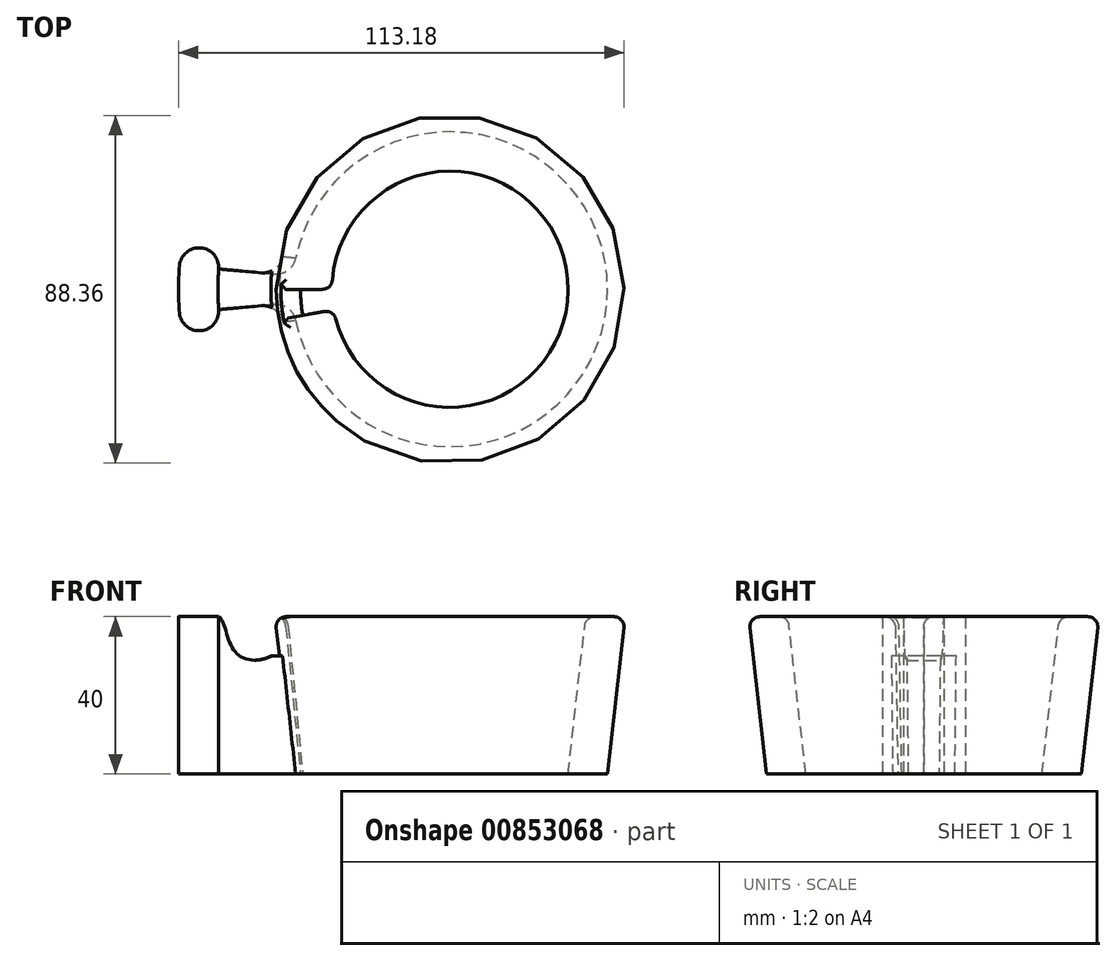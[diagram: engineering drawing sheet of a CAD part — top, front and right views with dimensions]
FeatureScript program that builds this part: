
annotation { "Feature Type Name" : "Feature", "Feature Type Description" : "" }
export const myFeature = defineFeature(function(context is Context, id is Id, definition is map)
    precondition{}
    {
        {
            var Q0;
            Q0=qCreatedBy(makeId("Front.planeOp"),FACE);
            var sketch = newSketch(context, id + "F0", { "sketchPlane" : qUnion([Q0])});
            skPoint(sketch, "E0", {"position": v(-30, 0) * mm});
            skPoint(sketch, "E1", {"position": v(-45, 134) * mm});
            skLineSegment(sketch, "E2", {"start": v(-34.48, 40) * mm, "end": v(-30, 0) * mm});
            skPoint(sketch, "E3", {"position": v(-34.48, 40) * mm});
            skLineSegment(sketch, "E4", {"start": v(-34.48, 40) * mm, "end": v(-44.48, 40) * mm});
            skLineSegment(sketch, "E5", {"start": v(-44.48, 40) * mm, "end": v(-40, 0) * mm});
            skLineSegment(sketch, "E6", {"start": v(-40, 0) * mm, "end": v(-30, 0) * mm});
            skLineSegment(sketch, "E7", {"start": v(0, 0) * mm, "end": v(0, 35.23) * mm});
            skSolve(sketch);
        }
        {
            var Q0;
            Q0=makeQuery(id+"F0.imprint","IMPRINT",FACE,{"disambiguationData":[TD([[makeQuery(id+"F0.imprint","IMPRINT",EDGE,{"derivedFrom":sQuery(id+"F0.wireOp",EDGE,"E2")}),-1.0]])]});
            var Q1;
            Q1=sQuery(id+"F0.wireOp",EDGE,"E7");
            revolve(context, id + "F1", {"surfaceOperationType" : NewSurfaceOperationType.NEW, "entities" : qUnion([Q0]), "axis" : qUnion([Q1]), "revolveType" : RevolveType.FULL});
        }
        {
            var Q0;
            Q0=qCreatedBy(makeId("Front.planeOp"),FACE);
            var sketch = newSketch(context, id + "F2", { "sketchPlane" : qUnion([Q0])});
            skPoint(sketch, "E8", {"position": v(-34, 40) * mm});
            skPoint(sketch, "E9", {"position": v(-30, 0) * mm});
            skLineSegment(sketch, "E10", {"start": v(-30, 0) * mm, "end": v(-34, 40) * mm});
            skLineSegment(sketch, "E11", {"start": v(-42, 40) * mm, "end": v(-38, 0) * mm});
            skLineSegment(sketch, "E12", {"start": v(-38, 0) * mm, "end": v(-30, 0) * mm});
            skLineSegment(sketch, "E13", {"start": v(-42, 40) * mm, "end": v(-34, 40) * mm});
            skSolve(sketch);
        }
        {
            var Q0;
            Q0 = qSketchRegion(id + "F2", true);
            var Q1;
            Q1=sQuery(id+"F0.wireOp",EDGE,"E7");
            revolve(context, id + "F3", {"operationType" : NewBodyOperationType.REMOVE, "surfaceOperationType" : NewSurfaceOperationType.NEW, "entities" : qUnion([Q0]), "axis" : qUnion([Q1]), "revolveType" : RevolveType.ONE_DIRECTION, "angle" : 10 * degree});
        }
        {
            var Q0;
            Q0=makeQuery(id+"F3.boolean.opBoolean","INTERSECT",EDGE,{"derivedFrom":[makeQuery(id+"F1.opRevolve","SWEPT_FACE",FACE,{"disambiguationData":[OSD([sQuery(id+"F0.wireOp",EDGE,"E2")])]}),makeQuery(id+"F3.opRevolve","CAP_FACE",FACE,{"disambiguationData":[OSD([sQuery(id+"F2.wireOp",EDGE,"E10"),sQuery(id+"F2.wireOp",EDGE,"E11"),sQuery(id+"F2.wireOp",EDGE,"E12"),sQuery(id+"F2.wireOp",EDGE,"E13")])],"isStart":true})]});
            var Q1;
            {var subQ0=sQuery(id+"F2.wireOp",EDGE,"E13");var subQ1=sQuery(id+"F2.wireOp",EDGE,"E12");var subQ2=sQuery(id+"F2.wireOp",EDGE,"E11");var subQ3=sQuery(id+"F2.wireOp",EDGE,"E10");var subQ6=makeQuery(id+"F3.boolean.opBoolean","COPY",FACE,{"derivedFrom":makeQuery(id+"F3.opRevolve","CAP_FACE",FACE,{"disambiguationData":[OSD([subQ3,subQ2,subQ1,subQ0])],"isStart":true})});Q1=makeQuery(id+"FKiHbmxaIrGreLf_1.19.F3.boolean.opBoolean","INTERSECT",EDGE,{"derivedFrom":[makeQuery(id+"FKiHbmxaIrGreLf_1.18.F3.boolean.opBoolean","SPLIT",FACE,{"disambiguationData":[TD([subQ6])],"derivedFrom":makeQuery(id+"FKiHbmxaIrGreLf_1.17.F3.boolean.opBoolean","SPLIT",FACE,{"disambiguationData":[TD([subQ6])],"derivedFrom":makeQuery(id+"FKiHbmxaIrGreLf_1.16.F3.boolean.opBoolean","SPLIT",FACE,{"disambiguationData":[TD([subQ6])],"derivedFrom":makeQuery(id+"FKiHbmxaIrGreLf_1.15.F3.boolean.opBoolean","SPLIT",FACE,{"disambiguationData":[TD([subQ6])],"derivedFrom":makeQuery(id+"FKiHbmxaIrGreLf_1.14.F3.boolean.opBoolean","SPLIT",FACE,{"disambiguationData":[TD([subQ6])],"derivedFrom":makeQuery(id+"FKiHbmxaIrGreLf_1.13.F3.boolean.opBoolean","SPLIT",FACE,{"disambiguationData":[TD([subQ6])],"derivedFrom":makeQuery(id+"FKiHbmxaIrGreLf_1.12.F3.boolean.opBoolean","SPLIT",FACE,{"disambiguationData":[TD([subQ6])],"derivedFrom":makeQuery(id+"FKiHbmxaIrGreLf_1.11.F3.boolean.opBoolean","SPLIT",FACE,{"disambiguationData":[TD([subQ6])],"derivedFrom":makeQuery(id+"FKiHbmxaIrGreLf_1.10.F3.boolean.opBoolean","SPLIT",FACE,{"disambiguationData":[TD([subQ6])],"derivedFrom":makeQuery(id+"FKiHbmxaIrGreLf_1.9.F3.boolean.opBoolean","SPLIT",FACE,{"disambiguationData":[TD([subQ6])],"derivedFrom":makeQuery(id+"FKiHbmxaIrGreLf_1.8.F3.boolean.opBoolean","SPLIT",FACE,{"disambiguationData":[TD([subQ6])],"derivedFrom":makeQuery(id+"FKiHbmxaIrGreLf_1.7.F3.boolean.opBoolean","SPLIT",FACE,{"disambiguationData":[TD([subQ6])],"derivedFrom":makeQuery(id+"FKiHbmxaIrGreLf_1.6.F3.boolean.opBoolean","SPLIT",FACE,{"disambiguationData":[TD([subQ6])],"derivedFrom":makeQuery(id+"FKiHbmxaIrGreLf_1.5.F3.boolean.opBoolean","SPLIT",FACE,{"disambiguationData":[TD([subQ6])],"derivedFrom":makeQuery(id+"FKiHbmxaIrGreLf_1.4.F3.boolean.opBoolean","SPLIT",FACE,{"disambiguationData":[TD([subQ6])],"derivedFrom":makeQuery(id+"FKiHbmxaIrGreLf_1.3.F3.boolean.opBoolean","SPLIT",FACE,{"disambiguationData":[TD([subQ6])],"derivedFrom":makeQuery(id+"FKiHbmxaIrGreLf_1.2.F3.boolean.opBoolean","SPLIT",FACE,{"disambiguationData":[TD([subQ6])],"derivedFrom":makeQuery(id+"FKiHbmxaIrGreLf_1.1.F3.boolean.opBoolean","SPLIT",FACE,{"disambiguationData":[TD([subQ6])],"derivedFrom":makeQuery(id+"F1.opRevolve","SWEPT_FACE",FACE,{"disambiguationData":[OSD([sQuery(id+"F0.wireOp",EDGE,"E2")])]})})})})})})})})})})})})})})})})})})}),makeQuery(id+"FKiHbmxaIrGreLf_1.19.F3.opRevolve","CAP_FACE",FACE,{"disambiguationData":[OSD([subQ3,subQ2,subQ1,subQ0])],"isStart":false})]});}
            var Q2;
            {var subQ0=sQuery(id+"F2.wireOp",EDGE,"E13");var subQ1=sQuery(id+"F2.wireOp",EDGE,"E12");var subQ2=sQuery(id+"F2.wireOp",EDGE,"E11");var subQ3=sQuery(id+"F2.wireOp",EDGE,"E10");var subQ6=makeQuery(id+"F3.boolean.opBoolean","COPY",FACE,{"derivedFrom":makeQuery(id+"F3.opRevolve","CAP_FACE",FACE,{"disambiguationData":[OSD([subQ3,subQ2,subQ1,subQ0])],"isStart":true})});Q2=makeQuery(id+"FKiHbmxaIrGreLf_1.19.F3.boolean.opBoolean","INTERSECT",EDGE,{"derivedFrom":[makeQuery(id+"FKiHbmxaIrGreLf_1.18.F3.boolean.opBoolean","SPLIT",FACE,{"disambiguationData":[TD([subQ6])],"derivedFrom":makeQuery(id+"FKiHbmxaIrGreLf_1.17.F3.boolean.opBoolean","SPLIT",FACE,{"disambiguationData":[TD([subQ6])],"derivedFrom":makeQuery(id+"FKiHbmxaIrGreLf_1.16.F3.boolean.opBoolean","SPLIT",FACE,{"disambiguationData":[TD([subQ6])],"derivedFrom":makeQuery(id+"FKiHbmxaIrGreLf_1.15.F3.boolean.opBoolean","SPLIT",FACE,{"disambiguationData":[TD([subQ6])],"derivedFrom":makeQuery(id+"FKiHbmxaIrGreLf_1.14.F3.boolean.opBoolean","SPLIT",FACE,{"disambiguationData":[TD([subQ6])],"derivedFrom":makeQuery(id+"FKiHbmxaIrGreLf_1.13.F3.boolean.opBoolean","SPLIT",FACE,{"disambiguationData":[TD([subQ6])],"derivedFrom":makeQuery(id+"FKiHbmxaIrGreLf_1.12.F3.boolean.opBoolean","SPLIT",FACE,{"disambiguationData":[TD([subQ6])],"derivedFrom":makeQuery(id+"FKiHbmxaIrGreLf_1.11.F3.boolean.opBoolean","SPLIT",FACE,{"disambiguationData":[TD([subQ6])],"derivedFrom":makeQuery(id+"FKiHbmxaIrGreLf_1.10.F3.boolean.opBoolean","SPLIT",FACE,{"disambiguationData":[TD([subQ6])],"derivedFrom":makeQuery(id+"FKiHbmxaIrGreLf_1.9.F3.boolean.opBoolean","SPLIT",FACE,{"disambiguationData":[TD([subQ6])],"derivedFrom":makeQuery(id+"FKiHbmxaIrGreLf_1.8.F3.boolean.opBoolean","SPLIT",FACE,{"disambiguationData":[TD([subQ6])],"derivedFrom":makeQuery(id+"FKiHbmxaIrGreLf_1.7.F3.boolean.opBoolean","SPLIT",FACE,{"disambiguationData":[TD([subQ6])],"derivedFrom":makeQuery(id+"FKiHbmxaIrGreLf_1.6.F3.boolean.opBoolean","SPLIT",FACE,{"disambiguationData":[TD([subQ6])],"derivedFrom":makeQuery(id+"FKiHbmxaIrGreLf_1.5.F3.boolean.opBoolean","SPLIT",FACE,{"disambiguationData":[TD([subQ6])],"derivedFrom":makeQuery(id+"FKiHbmxaIrGreLf_1.4.F3.boolean.opBoolean","SPLIT",FACE,{"disambiguationData":[TD([subQ6])],"derivedFrom":makeQuery(id+"FKiHbmxaIrGreLf_1.3.F3.boolean.opBoolean","SPLIT",FACE,{"disambiguationData":[TD([subQ6])],"derivedFrom":makeQuery(id+"FKiHbmxaIrGreLf_1.2.F3.boolean.opBoolean","SPLIT",FACE,{"disambiguationData":[TD([subQ6])],"derivedFrom":makeQuery(id+"FKiHbmxaIrGreLf_1.1.F3.boolean.opBoolean","SPLIT",FACE,{"disambiguationData":[TD([subQ6])],"derivedFrom":makeQuery(id+"F1.opRevolve","SWEPT_FACE",FACE,{"disambiguationData":[OSD([sQuery(id+"F0.wireOp",EDGE,"E2")])]})})})})})})})})})})})})})})})})})})}),makeQuery(id+"FKiHbmxaIrGreLf_1.19.F3.opRevolve","CAP_FACE",FACE,{"disambiguationData":[OSD([subQ3,subQ2,subQ1,subQ0])],"isStart":true})]});}
            var Q3;
            {var subQ0=sQuery(id+"F2.wireOp",EDGE,"E13");var subQ1=sQuery(id+"F2.wireOp",EDGE,"E12");var subQ2=sQuery(id+"F2.wireOp",EDGE,"E11");var subQ3=sQuery(id+"F2.wireOp",EDGE,"E10");var subQ6=makeQuery(id+"F3.boolean.opBoolean","COPY",FACE,{"derivedFrom":makeQuery(id+"F3.opRevolve","CAP_FACE",FACE,{"disambiguationData":[OSD([subQ3,subQ2,subQ1,subQ0])],"isStart":true})});Q3=makeQuery(id+"FKiHbmxaIrGreLf_1.18.F3.boolean.opBoolean","INTERSECT",EDGE,{"derivedFrom":[makeQuery(id+"FKiHbmxaIrGreLf_1.17.F3.boolean.opBoolean","SPLIT",FACE,{"disambiguationData":[TD([subQ6])],"derivedFrom":makeQuery(id+"FKiHbmxaIrGreLf_1.16.F3.boolean.opBoolean","SPLIT",FACE,{"disambiguationData":[TD([subQ6])],"derivedFrom":makeQuery(id+"FKiHbmxaIrGreLf_1.15.F3.boolean.opBoolean","SPLIT",FACE,{"disambiguationData":[TD([subQ6])],"derivedFrom":makeQuery(id+"FKiHbmxaIrGreLf_1.14.F3.boolean.opBoolean","SPLIT",FACE,{"disambiguationData":[TD([subQ6])],"derivedFrom":makeQuery(id+"FKiHbmxaIrGreLf_1.13.F3.boolean.opBoolean","SPLIT",FACE,{"disambiguationData":[TD([subQ6])],"derivedFrom":makeQuery(id+"FKiHbmxaIrGreLf_1.12.F3.boolean.opBoolean","SPLIT",FACE,{"disambiguationData":[TD([subQ6])],"derivedFrom":makeQuery(id+"FKiHbmxaIrGreLf_1.11.F3.boolean.opBoolean","SPLIT",FACE,{"disambiguationData":[TD([subQ6])],"derivedFrom":makeQuery(id+"FKiHbmxaIrGreLf_1.10.F3.boolean.opBoolean","SPLIT",FACE,{"disambiguationData":[TD([subQ6])],"derivedFrom":makeQuery(id+"FKiHbmxaIrGreLf_1.9.F3.boolean.opBoolean","SPLIT",FACE,{"disambiguationData":[TD([subQ6])],"derivedFrom":makeQuery(id+"FKiHbmxaIrGreLf_1.8.F3.boolean.opBoolean","SPLIT",FACE,{"disambiguationData":[TD([subQ6])],"derivedFrom":makeQuery(id+"FKiHbmxaIrGreLf_1.7.F3.boolean.opBoolean","SPLIT",FACE,{"disambiguationData":[TD([subQ6])],"derivedFrom":makeQuery(id+"FKiHbmxaIrGreLf_1.6.F3.boolean.opBoolean","SPLIT",FACE,{"disambiguationData":[TD([subQ6])],"derivedFrom":makeQuery(id+"FKiHbmxaIrGreLf_1.5.F3.boolean.opBoolean","SPLIT",FACE,{"disambiguationData":[TD([subQ6])],"derivedFrom":makeQuery(id+"FKiHbmxaIrGreLf_1.4.F3.boolean.opBoolean","SPLIT",FACE,{"disambiguationData":[TD([subQ6])],"derivedFrom":makeQuery(id+"FKiHbmxaIrGreLf_1.3.F3.boolean.opBoolean","SPLIT",FACE,{"disambiguationData":[TD([subQ6])],"derivedFrom":makeQuery(id+"FKiHbmxaIrGreLf_1.2.F3.boolean.opBoolean","SPLIT",FACE,{"disambiguationData":[TD([subQ6])],"derivedFrom":makeQuery(id+"FKiHbmxaIrGreLf_1.1.F3.boolean.opBoolean","SPLIT",FACE,{"disambiguationData":[TD([subQ6])],"derivedFrom":makeQuery(id+"F1.opRevolve","SWEPT_FACE",FACE,{"disambiguationData":[OSD([sQuery(id+"F0.wireOp",EDGE,"E2")])]})})})})})})})})})})})})})})})})})}),makeQuery(id+"FKiHbmxaIrGreLf_1.18.F3.opRevolve","CAP_FACE",FACE,{"disambiguationData":[OSD([subQ3,subQ2,subQ1,subQ0])],"isStart":false})]});}
            var Q4;
            {var subQ0=sQuery(id+"F2.wireOp",EDGE,"E13");var subQ1=sQuery(id+"F2.wireOp",EDGE,"E12");var subQ2=sQuery(id+"F2.wireOp",EDGE,"E11");var subQ3=sQuery(id+"F2.wireOp",EDGE,"E10");var subQ6=makeQuery(id+"F3.boolean.opBoolean","COPY",FACE,{"derivedFrom":makeQuery(id+"F3.opRevolve","CAP_FACE",FACE,{"disambiguationData":[OSD([subQ3,subQ2,subQ1,subQ0])],"isStart":true})});Q4=makeQuery(id+"FKiHbmxaIrGreLf_1.18.F3.boolean.opBoolean","INTERSECT",EDGE,{"derivedFrom":[makeQuery(id+"FKiHbmxaIrGreLf_1.17.F3.boolean.opBoolean","SPLIT",FACE,{"disambiguationData":[TD([subQ6])],"derivedFrom":makeQuery(id+"FKiHbmxaIrGreLf_1.16.F3.boolean.opBoolean","SPLIT",FACE,{"disambiguationData":[TD([subQ6])],"derivedFrom":makeQuery(id+"FKiHbmxaIrGreLf_1.15.F3.boolean.opBoolean","SPLIT",FACE,{"disambiguationData":[TD([subQ6])],"derivedFrom":makeQuery(id+"FKiHbmxaIrGreLf_1.14.F3.boolean.opBoolean","SPLIT",FACE,{"disambiguationData":[TD([subQ6])],"derivedFrom":makeQuery(id+"FKiHbmxaIrGreLf_1.13.F3.boolean.opBoolean","SPLIT",FACE,{"disambiguationData":[TD([subQ6])],"derivedFrom":makeQuery(id+"FKiHbmxaIrGreLf_1.12.F3.boolean.opBoolean","SPLIT",FACE,{"disambiguationData":[TD([subQ6])],"derivedFrom":makeQuery(id+"FKiHbmxaIrGreLf_1.11.F3.boolean.opBoolean","SPLIT",FACE,{"disambiguationData":[TD([subQ6])],"derivedFrom":makeQuery(id+"FKiHbmxaIrGreLf_1.10.F3.boolean.opBoolean","SPLIT",FACE,{"disambiguationData":[TD([subQ6])],"derivedFrom":makeQuery(id+"FKiHbmxaIrGreLf_1.9.F3.boolean.opBoolean","SPLIT",FACE,{"disambiguationData":[TD([subQ6])],"derivedFrom":makeQuery(id+"FKiHbmxaIrGreLf_1.8.F3.boolean.opBoolean","SPLIT",FACE,{"disambiguationData":[TD([subQ6])],"derivedFrom":makeQuery(id+"FKiHbmxaIrGreLf_1.7.F3.boolean.opBoolean","SPLIT",FACE,{"disambiguationData":[TD([subQ6])],"derivedFrom":makeQuery(id+"FKiHbmxaIrGreLf_1.6.F3.boolean.opBoolean","SPLIT",FACE,{"disambiguationData":[TD([subQ6])],"derivedFrom":makeQuery(id+"FKiHbmxaIrGreLf_1.5.F3.boolean.opBoolean","SPLIT",FACE,{"disambiguationData":[TD([subQ6])],"derivedFrom":makeQuery(id+"FKiHbmxaIrGreLf_1.4.F3.boolean.opBoolean","SPLIT",FACE,{"disambiguationData":[TD([subQ6])],"derivedFrom":makeQuery(id+"FKiHbmxaIrGreLf_1.3.F3.boolean.opBoolean","SPLIT",FACE,{"disambiguationData":[TD([subQ6])],"derivedFrom":makeQuery(id+"FKiHbmxaIrGreLf_1.2.F3.boolean.opBoolean","SPLIT",FACE,{"disambiguationData":[TD([subQ6])],"derivedFrom":makeQuery(id+"FKiHbmxaIrGreLf_1.1.F3.boolean.opBoolean","SPLIT",FACE,{"disambiguationData":[TD([subQ6])],"derivedFrom":makeQuery(id+"F1.opRevolve","SWEPT_FACE",FACE,{"disambiguationData":[OSD([sQuery(id+"F0.wireOp",EDGE,"E2")])]})})})})})})})})})})})})})})})})})}),makeQuery(id+"FKiHbmxaIrGreLf_1.18.F3.opRevolve","CAP_FACE",FACE,{"disambiguationData":[OSD([subQ3,subQ2,subQ1,subQ0])],"isStart":true})]});}
            var Q5;
            {var subQ0=sQuery(id+"F2.wireOp",EDGE,"E13");var subQ1=sQuery(id+"F2.wireOp",EDGE,"E12");var subQ2=sQuery(id+"F2.wireOp",EDGE,"E11");var subQ3=sQuery(id+"F2.wireOp",EDGE,"E10");var subQ6=makeQuery(id+"F3.boolean.opBoolean","COPY",FACE,{"derivedFrom":makeQuery(id+"F3.opRevolve","CAP_FACE",FACE,{"disambiguationData":[OSD([subQ3,subQ2,subQ1,subQ0])],"isStart":true})});Q5=makeQuery(id+"FKiHbmxaIrGreLf_1.17.F3.boolean.opBoolean","INTERSECT",EDGE,{"derivedFrom":[makeQuery(id+"FKiHbmxaIrGreLf_1.16.F3.boolean.opBoolean","SPLIT",FACE,{"disambiguationData":[TD([subQ6])],"derivedFrom":makeQuery(id+"FKiHbmxaIrGreLf_1.15.F3.boolean.opBoolean","SPLIT",FACE,{"disambiguationData":[TD([subQ6])],"derivedFrom":makeQuery(id+"FKiHbmxaIrGreLf_1.14.F3.boolean.opBoolean","SPLIT",FACE,{"disambiguationData":[TD([subQ6])],"derivedFrom":makeQuery(id+"FKiHbmxaIrGreLf_1.13.F3.boolean.opBoolean","SPLIT",FACE,{"disambiguationData":[TD([subQ6])],"derivedFrom":makeQuery(id+"FKiHbmxaIrGreLf_1.12.F3.boolean.opBoolean","SPLIT",FACE,{"disambiguationData":[TD([subQ6])],"derivedFrom":makeQuery(id+"FKiHbmxaIrGreLf_1.11.F3.boolean.opBoolean","SPLIT",FACE,{"disambiguationData":[TD([subQ6])],"derivedFrom":makeQuery(id+"FKiHbmxaIrGreLf_1.10.F3.boolean.opBoolean","SPLIT",FACE,{"disambiguationData":[TD([subQ6])],"derivedFrom":makeQuery(id+"FKiHbmxaIrGreLf_1.9.F3.boolean.opBoolean","SPLIT",FACE,{"disambiguationData":[TD([subQ6])],"derivedFrom":makeQuery(id+"FKiHbmxaIrGreLf_1.8.F3.boolean.opBoolean","SPLIT",FACE,{"disambiguationData":[TD([subQ6])],"derivedFrom":makeQuery(id+"FKiHbmxaIrGreLf_1.7.F3.boolean.opBoolean","SPLIT",FACE,{"disambiguationData":[TD([subQ6])],"derivedFrom":makeQuery(id+"FKiHbmxaIrGreLf_1.6.F3.boolean.opBoolean","SPLIT",FACE,{"disambiguationData":[TD([subQ6])],"derivedFrom":makeQuery(id+"FKiHbmxaIrGreLf_1.5.F3.boolean.opBoolean","SPLIT",FACE,{"disambiguationData":[TD([subQ6])],"derivedFrom":makeQuery(id+"FKiHbmxaIrGreLf_1.4.F3.boolean.opBoolean","SPLIT",FACE,{"disambiguationData":[TD([subQ6])],"derivedFrom":makeQuery(id+"FKiHbmxaIrGreLf_1.3.F3.boolean.opBoolean","SPLIT",FACE,{"disambiguationData":[TD([subQ6])],"derivedFrom":makeQuery(id+"FKiHbmxaIrGreLf_1.2.F3.boolean.opBoolean","SPLIT",FACE,{"disambiguationData":[TD([subQ6])],"derivedFrom":makeQuery(id+"FKiHbmxaIrGreLf_1.1.F3.boolean.opBoolean","SPLIT",FACE,{"disambiguationData":[TD([subQ6])],"derivedFrom":makeQuery(id+"F1.opRevolve","SWEPT_FACE",FACE,{"disambiguationData":[OSD([sQuery(id+"F0.wireOp",EDGE,"E2")])]})})})})})})})})})})})})})})})})}),makeQuery(id+"FKiHbmxaIrGreLf_1.17.F3.opRevolve","CAP_FACE",FACE,{"disambiguationData":[OSD([subQ3,subQ2,subQ1,subQ0])],"isStart":false})]});}
            var Q6;
            {var subQ0=sQuery(id+"F2.wireOp",EDGE,"E13");var subQ1=sQuery(id+"F2.wireOp",EDGE,"E12");var subQ2=sQuery(id+"F2.wireOp",EDGE,"E11");var subQ3=sQuery(id+"F2.wireOp",EDGE,"E10");var subQ6=makeQuery(id+"F3.boolean.opBoolean","COPY",FACE,{"derivedFrom":makeQuery(id+"F3.opRevolve","CAP_FACE",FACE,{"disambiguationData":[OSD([subQ3,subQ2,subQ1,subQ0])],"isStart":true})});Q6=makeQuery(id+"FKiHbmxaIrGreLf_1.17.F3.boolean.opBoolean","INTERSECT",EDGE,{"derivedFrom":[makeQuery(id+"FKiHbmxaIrGreLf_1.16.F3.boolean.opBoolean","SPLIT",FACE,{"disambiguationData":[TD([subQ6])],"derivedFrom":makeQuery(id+"FKiHbmxaIrGreLf_1.15.F3.boolean.opBoolean","SPLIT",FACE,{"disambiguationData":[TD([subQ6])],"derivedFrom":makeQuery(id+"FKiHbmxaIrGreLf_1.14.F3.boolean.opBoolean","SPLIT",FACE,{"disambiguationData":[TD([subQ6])],"derivedFrom":makeQuery(id+"FKiHbmxaIrGreLf_1.13.F3.boolean.opBoolean","SPLIT",FACE,{"disambiguationData":[TD([subQ6])],"derivedFrom":makeQuery(id+"FKiHbmxaIrGreLf_1.12.F3.boolean.opBoolean","SPLIT",FACE,{"disambiguationData":[TD([subQ6])],"derivedFrom":makeQuery(id+"FKiHbmxaIrGreLf_1.11.F3.boolean.opBoolean","SPLIT",FACE,{"disambiguationData":[TD([subQ6])],"derivedFrom":makeQuery(id+"FKiHbmxaIrGreLf_1.10.F3.boolean.opBoolean","SPLIT",FACE,{"disambiguationData":[TD([subQ6])],"derivedFrom":makeQuery(id+"FKiHbmxaIrGreLf_1.9.F3.boolean.opBoolean","SPLIT",FACE,{"disambiguationData":[TD([subQ6])],"derivedFrom":makeQuery(id+"FKiHbmxaIrGreLf_1.8.F3.boolean.opBoolean","SPLIT",FACE,{"disambiguationData":[TD([subQ6])],"derivedFrom":makeQuery(id+"FKiHbmxaIrGreLf_1.7.F3.boolean.opBoolean","SPLIT",FACE,{"disambiguationData":[TD([subQ6])],"derivedFrom":makeQuery(id+"FKiHbmxaIrGreLf_1.6.F3.boolean.opBoolean","SPLIT",FACE,{"disambiguationData":[TD([subQ6])],"derivedFrom":makeQuery(id+"FKiHbmxaIrGreLf_1.5.F3.boolean.opBoolean","SPLIT",FACE,{"disambiguationData":[TD([subQ6])],"derivedFrom":makeQuery(id+"FKiHbmxaIrGreLf_1.4.F3.boolean.opBoolean","SPLIT",FACE,{"disambiguationData":[TD([subQ6])],"derivedFrom":makeQuery(id+"FKiHbmxaIrGreLf_1.3.F3.boolean.opBoolean","SPLIT",FACE,{"disambiguationData":[TD([subQ6])],"derivedFrom":makeQuery(id+"FKiHbmxaIrGreLf_1.2.F3.boolean.opBoolean","SPLIT",FACE,{"disambiguationData":[TD([subQ6])],"derivedFrom":makeQuery(id+"FKiHbmxaIrGreLf_1.1.F3.boolean.opBoolean","SPLIT",FACE,{"disambiguationData":[TD([subQ6])],"derivedFrom":makeQuery(id+"F1.opRevolve","SWEPT_FACE",FACE,{"disambiguationData":[OSD([sQuery(id+"F0.wireOp",EDGE,"E2")])]})})})})})})})})})})})})})})})})}),makeQuery(id+"FKiHbmxaIrGreLf_1.17.F3.opRevolve","CAP_FACE",FACE,{"disambiguationData":[OSD([subQ3,subQ2,subQ1,subQ0])],"isStart":true})]});}
            var Q7;
            {var subQ0=sQuery(id+"F2.wireOp",EDGE,"E13");var subQ1=sQuery(id+"F2.wireOp",EDGE,"E12");var subQ2=sQuery(id+"F2.wireOp",EDGE,"E11");var subQ3=sQuery(id+"F2.wireOp",EDGE,"E10");var subQ6=makeQuery(id+"F3.boolean.opBoolean","COPY",FACE,{"derivedFrom":makeQuery(id+"F3.opRevolve","CAP_FACE",FACE,{"disambiguationData":[OSD([subQ3,subQ2,subQ1,subQ0])],"isStart":true})});Q7=makeQuery(id+"FKiHbmxaIrGreLf_1.16.F3.boolean.opBoolean","INTERSECT",EDGE,{"derivedFrom":[makeQuery(id+"FKiHbmxaIrGreLf_1.15.F3.boolean.opBoolean","SPLIT",FACE,{"disambiguationData":[TD([subQ6])],"derivedFrom":makeQuery(id+"FKiHbmxaIrGreLf_1.14.F3.boolean.opBoolean","SPLIT",FACE,{"disambiguationData":[TD([subQ6])],"derivedFrom":makeQuery(id+"FKiHbmxaIrGreLf_1.13.F3.boolean.opBoolean","SPLIT",FACE,{"disambiguationData":[TD([subQ6])],"derivedFrom":makeQuery(id+"FKiHbmxaIrGreLf_1.12.F3.boolean.opBoolean","SPLIT",FACE,{"disambiguationData":[TD([subQ6])],"derivedFrom":makeQuery(id+"FKiHbmxaIrGreLf_1.11.F3.boolean.opBoolean","SPLIT",FACE,{"disambiguationData":[TD([subQ6])],"derivedFrom":makeQuery(id+"FKiHbmxaIrGreLf_1.10.F3.boolean.opBoolean","SPLIT",FACE,{"disambiguationData":[TD([subQ6])],"derivedFrom":makeQuery(id+"FKiHbmxaIrGreLf_1.9.F3.boolean.opBoolean","SPLIT",FACE,{"disambiguationData":[TD([subQ6])],"derivedFrom":makeQuery(id+"FKiHbmxaIrGreLf_1.8.F3.boolean.opBoolean","SPLIT",FACE,{"disambiguationData":[TD([subQ6])],"derivedFrom":makeQuery(id+"FKiHbmxaIrGreLf_1.7.F3.boolean.opBoolean","SPLIT",FACE,{"disambiguationData":[TD([subQ6])],"derivedFrom":makeQuery(id+"FKiHbmxaIrGreLf_1.6.F3.boolean.opBoolean","SPLIT",FACE,{"disambiguationData":[TD([subQ6])],"derivedFrom":makeQuery(id+"FKiHbmxaIrGreLf_1.5.F3.boolean.opBoolean","SPLIT",FACE,{"disambiguationData":[TD([subQ6])],"derivedFrom":makeQuery(id+"FKiHbmxaIrGreLf_1.4.F3.boolean.opBoolean","SPLIT",FACE,{"disambiguationData":[TD([subQ6])],"derivedFrom":makeQuery(id+"FKiHbmxaIrGreLf_1.3.F3.boolean.opBoolean","SPLIT",FACE,{"disambiguationData":[TD([subQ6])],"derivedFrom":makeQuery(id+"FKiHbmxaIrGreLf_1.2.F3.boolean.opBoolean","SPLIT",FACE,{"disambiguationData":[TD([subQ6])],"derivedFrom":makeQuery(id+"FKiHbmxaIrGreLf_1.1.F3.boolean.opBoolean","SPLIT",FACE,{"disambiguationData":[TD([subQ6])],"derivedFrom":makeQuery(id+"F1.opRevolve","SWEPT_FACE",FACE,{"disambiguationData":[OSD([sQuery(id+"F0.wireOp",EDGE,"E2")])]})})})})})})})})})})})})})})})}),makeQuery(id+"FKiHbmxaIrGreLf_1.16.F3.opRevolve","CAP_FACE",FACE,{"disambiguationData":[OSD([subQ3,subQ2,subQ1,subQ0])],"isStart":false})]});}
            var Q8;
            {var subQ0=sQuery(id+"F2.wireOp",EDGE,"E13");var subQ1=sQuery(id+"F2.wireOp",EDGE,"E12");var subQ2=sQuery(id+"F2.wireOp",EDGE,"E11");var subQ3=sQuery(id+"F2.wireOp",EDGE,"E10");var subQ6=makeQuery(id+"F3.boolean.opBoolean","COPY",FACE,{"derivedFrom":makeQuery(id+"F3.opRevolve","CAP_FACE",FACE,{"disambiguationData":[OSD([subQ3,subQ2,subQ1,subQ0])],"isStart":true})});Q8=makeQuery(id+"FKiHbmxaIrGreLf_1.16.F3.boolean.opBoolean","INTERSECT",EDGE,{"derivedFrom":[makeQuery(id+"FKiHbmxaIrGreLf_1.15.F3.boolean.opBoolean","SPLIT",FACE,{"disambiguationData":[TD([subQ6])],"derivedFrom":makeQuery(id+"FKiHbmxaIrGreLf_1.14.F3.boolean.opBoolean","SPLIT",FACE,{"disambiguationData":[TD([subQ6])],"derivedFrom":makeQuery(id+"FKiHbmxaIrGreLf_1.13.F3.boolean.opBoolean","SPLIT",FACE,{"disambiguationData":[TD([subQ6])],"derivedFrom":makeQuery(id+"FKiHbmxaIrGreLf_1.12.F3.boolean.opBoolean","SPLIT",FACE,{"disambiguationData":[TD([subQ6])],"derivedFrom":makeQuery(id+"FKiHbmxaIrGreLf_1.11.F3.boolean.opBoolean","SPLIT",FACE,{"disambiguationData":[TD([subQ6])],"derivedFrom":makeQuery(id+"FKiHbmxaIrGreLf_1.10.F3.boolean.opBoolean","SPLIT",FACE,{"disambiguationData":[TD([subQ6])],"derivedFrom":makeQuery(id+"FKiHbmxaIrGreLf_1.9.F3.boolean.opBoolean","SPLIT",FACE,{"disambiguationData":[TD([subQ6])],"derivedFrom":makeQuery(id+"FKiHbmxaIrGreLf_1.8.F3.boolean.opBoolean","SPLIT",FACE,{"disambiguationData":[TD([subQ6])],"derivedFrom":makeQuery(id+"FKiHbmxaIrGreLf_1.7.F3.boolean.opBoolean","SPLIT",FACE,{"disambiguationData":[TD([subQ6])],"derivedFrom":makeQuery(id+"FKiHbmxaIrGreLf_1.6.F3.boolean.opBoolean","SPLIT",FACE,{"disambiguationData":[TD([subQ6])],"derivedFrom":makeQuery(id+"FKiHbmxaIrGreLf_1.5.F3.boolean.opBoolean","SPLIT",FACE,{"disambiguationData":[TD([subQ6])],"derivedFrom":makeQuery(id+"FKiHbmxaIrGreLf_1.4.F3.boolean.opBoolean","SPLIT",FACE,{"disambiguationData":[TD([subQ6])],"derivedFrom":makeQuery(id+"FKiHbmxaIrGreLf_1.3.F3.boolean.opBoolean","SPLIT",FACE,{"disambiguationData":[TD([subQ6])],"derivedFrom":makeQuery(id+"FKiHbmxaIrGreLf_1.2.F3.boolean.opBoolean","SPLIT",FACE,{"disambiguationData":[TD([subQ6])],"derivedFrom":makeQuery(id+"FKiHbmxaIrGreLf_1.1.F3.boolean.opBoolean","SPLIT",FACE,{"disambiguationData":[TD([subQ6])],"derivedFrom":makeQuery(id+"F1.opRevolve","SWEPT_FACE",FACE,{"disambiguationData":[OSD([sQuery(id+"F0.wireOp",EDGE,"E2")])]})})})})})})})})})})})})})})})}),makeQuery(id+"FKiHbmxaIrGreLf_1.16.F3.opRevolve","CAP_FACE",FACE,{"disambiguationData":[OSD([subQ3,subQ2,subQ1,subQ0])],"isStart":true})]});}
            var Q9;
            {var subQ0=sQuery(id+"F2.wireOp",EDGE,"E13");var subQ1=sQuery(id+"F2.wireOp",EDGE,"E12");var subQ2=sQuery(id+"F2.wireOp",EDGE,"E11");var subQ3=sQuery(id+"F2.wireOp",EDGE,"E10");var subQ6=makeQuery(id+"F3.boolean.opBoolean","COPY",FACE,{"derivedFrom":makeQuery(id+"F3.opRevolve","CAP_FACE",FACE,{"disambiguationData":[OSD([subQ3,subQ2,subQ1,subQ0])],"isStart":true})});Q9=makeQuery(id+"FKiHbmxaIrGreLf_1.15.F3.boolean.opBoolean","INTERSECT",EDGE,{"derivedFrom":[makeQuery(id+"FKiHbmxaIrGreLf_1.14.F3.boolean.opBoolean","SPLIT",FACE,{"disambiguationData":[TD([subQ6])],"derivedFrom":makeQuery(id+"FKiHbmxaIrGreLf_1.13.F3.boolean.opBoolean","SPLIT",FACE,{"disambiguationData":[TD([subQ6])],"derivedFrom":makeQuery(id+"FKiHbmxaIrGreLf_1.12.F3.boolean.opBoolean","SPLIT",FACE,{"disambiguationData":[TD([subQ6])],"derivedFrom":makeQuery(id+"FKiHbmxaIrGreLf_1.11.F3.boolean.opBoolean","SPLIT",FACE,{"disambiguationData":[TD([subQ6])],"derivedFrom":makeQuery(id+"FKiHbmxaIrGreLf_1.10.F3.boolean.opBoolean","SPLIT",FACE,{"disambiguationData":[TD([subQ6])],"derivedFrom":makeQuery(id+"FKiHbmxaIrGreLf_1.9.F3.boolean.opBoolean","SPLIT",FACE,{"disambiguationData":[TD([subQ6])],"derivedFrom":makeQuery(id+"FKiHbmxaIrGreLf_1.8.F3.boolean.opBoolean","SPLIT",FACE,{"disambiguationData":[TD([subQ6])],"derivedFrom":makeQuery(id+"FKiHbmxaIrGreLf_1.7.F3.boolean.opBoolean","SPLIT",FACE,{"disambiguationData":[TD([subQ6])],"derivedFrom":makeQuery(id+"FKiHbmxaIrGreLf_1.6.F3.boolean.opBoolean","SPLIT",FACE,{"disambiguationData":[TD([subQ6])],"derivedFrom":makeQuery(id+"FKiHbmxaIrGreLf_1.5.F3.boolean.opBoolean","SPLIT",FACE,{"disambiguationData":[TD([subQ6])],"derivedFrom":makeQuery(id+"FKiHbmxaIrGreLf_1.4.F3.boolean.opBoolean","SPLIT",FACE,{"disambiguationData":[TD([subQ6])],"derivedFrom":makeQuery(id+"FKiHbmxaIrGreLf_1.3.F3.boolean.opBoolean","SPLIT",FACE,{"disambiguationData":[TD([subQ6])],"derivedFrom":makeQuery(id+"FKiHbmxaIrGreLf_1.2.F3.boolean.opBoolean","SPLIT",FACE,{"disambiguationData":[TD([subQ6])],"derivedFrom":makeQuery(id+"FKiHbmxaIrGreLf_1.1.F3.boolean.opBoolean","SPLIT",FACE,{"disambiguationData":[TD([subQ6])],"derivedFrom":makeQuery(id+"F1.opRevolve","SWEPT_FACE",FACE,{"disambiguationData":[OSD([sQuery(id+"F0.wireOp",EDGE,"E2")])]})})})})})})})})})})})})})})}),makeQuery(id+"FKiHbmxaIrGreLf_1.15.F3.opRevolve","CAP_FACE",FACE,{"disambiguationData":[OSD([subQ3,subQ2,subQ1,subQ0])],"isStart":false})]});}
            var Q10;
            {var subQ0=sQuery(id+"F2.wireOp",EDGE,"E13");var subQ1=sQuery(id+"F2.wireOp",EDGE,"E12");var subQ2=sQuery(id+"F2.wireOp",EDGE,"E11");var subQ3=sQuery(id+"F2.wireOp",EDGE,"E10");var subQ6=makeQuery(id+"F3.boolean.opBoolean","COPY",FACE,{"derivedFrom":makeQuery(id+"F3.opRevolve","CAP_FACE",FACE,{"disambiguationData":[OSD([subQ3,subQ2,subQ1,subQ0])],"isStart":true})});Q10=makeQuery(id+"FKiHbmxaIrGreLf_1.15.F3.boolean.opBoolean","INTERSECT",EDGE,{"derivedFrom":[makeQuery(id+"FKiHbmxaIrGreLf_1.14.F3.boolean.opBoolean","SPLIT",FACE,{"disambiguationData":[TD([subQ6])],"derivedFrom":makeQuery(id+"FKiHbmxaIrGreLf_1.13.F3.boolean.opBoolean","SPLIT",FACE,{"disambiguationData":[TD([subQ6])],"derivedFrom":makeQuery(id+"FKiHbmxaIrGreLf_1.12.F3.boolean.opBoolean","SPLIT",FACE,{"disambiguationData":[TD([subQ6])],"derivedFrom":makeQuery(id+"FKiHbmxaIrGreLf_1.11.F3.boolean.opBoolean","SPLIT",FACE,{"disambiguationData":[TD([subQ6])],"derivedFrom":makeQuery(id+"FKiHbmxaIrGreLf_1.10.F3.boolean.opBoolean","SPLIT",FACE,{"disambiguationData":[TD([subQ6])],"derivedFrom":makeQuery(id+"FKiHbmxaIrGreLf_1.9.F3.boolean.opBoolean","SPLIT",FACE,{"disambiguationData":[TD([subQ6])],"derivedFrom":makeQuery(id+"FKiHbmxaIrGreLf_1.8.F3.boolean.opBoolean","SPLIT",FACE,{"disambiguationData":[TD([subQ6])],"derivedFrom":makeQuery(id+"FKiHbmxaIrGreLf_1.7.F3.boolean.opBoolean","SPLIT",FACE,{"disambiguationData":[TD([subQ6])],"derivedFrom":makeQuery(id+"FKiHbmxaIrGreLf_1.6.F3.boolean.opBoolean","SPLIT",FACE,{"disambiguationData":[TD([subQ6])],"derivedFrom":makeQuery(id+"FKiHbmxaIrGreLf_1.5.F3.boolean.opBoolean","SPLIT",FACE,{"disambiguationData":[TD([subQ6])],"derivedFrom":makeQuery(id+"FKiHbmxaIrGreLf_1.4.F3.boolean.opBoolean","SPLIT",FACE,{"disambiguationData":[TD([subQ6])],"derivedFrom":makeQuery(id+"FKiHbmxaIrGreLf_1.3.F3.boolean.opBoolean","SPLIT",FACE,{"disambiguationData":[TD([subQ6])],"derivedFrom":makeQuery(id+"FKiHbmxaIrGreLf_1.2.F3.boolean.opBoolean","SPLIT",FACE,{"disambiguationData":[TD([subQ6])],"derivedFrom":makeQuery(id+"FKiHbmxaIrGreLf_1.1.F3.boolean.opBoolean","SPLIT",FACE,{"disambiguationData":[TD([subQ6])],"derivedFrom":makeQuery(id+"F1.opRevolve","SWEPT_FACE",FACE,{"disambiguationData":[OSD([sQuery(id+"F0.wireOp",EDGE,"E2")])]})})})})})})})})})})})})})})}),makeQuery(id+"FKiHbmxaIrGreLf_1.15.F3.opRevolve","CAP_FACE",FACE,{"disambiguationData":[OSD([subQ3,subQ2,subQ1,subQ0])],"isStart":true})]});}
            var Q11;
            {var subQ0=sQuery(id+"F2.wireOp",EDGE,"E13");var subQ1=sQuery(id+"F2.wireOp",EDGE,"E12");var subQ2=sQuery(id+"F2.wireOp",EDGE,"E11");var subQ3=sQuery(id+"F2.wireOp",EDGE,"E10");var subQ6=makeQuery(id+"F3.boolean.opBoolean","COPY",FACE,{"derivedFrom":makeQuery(id+"F3.opRevolve","CAP_FACE",FACE,{"disambiguationData":[OSD([subQ3,subQ2,subQ1,subQ0])],"isStart":true})});Q11=makeQuery(id+"FKiHbmxaIrGreLf_1.14.F3.boolean.opBoolean","INTERSECT",EDGE,{"derivedFrom":[makeQuery(id+"FKiHbmxaIrGreLf_1.13.F3.boolean.opBoolean","SPLIT",FACE,{"disambiguationData":[TD([subQ6])],"derivedFrom":makeQuery(id+"FKiHbmxaIrGreLf_1.12.F3.boolean.opBoolean","SPLIT",FACE,{"disambiguationData":[TD([subQ6])],"derivedFrom":makeQuery(id+"FKiHbmxaIrGreLf_1.11.F3.boolean.opBoolean","SPLIT",FACE,{"disambiguationData":[TD([subQ6])],"derivedFrom":makeQuery(id+"FKiHbmxaIrGreLf_1.10.F3.boolean.opBoolean","SPLIT",FACE,{"disambiguationData":[TD([subQ6])],"derivedFrom":makeQuery(id+"FKiHbmxaIrGreLf_1.9.F3.boolean.opBoolean","SPLIT",FACE,{"disambiguationData":[TD([subQ6])],"derivedFrom":makeQuery(id+"FKiHbmxaIrGreLf_1.8.F3.boolean.opBoolean","SPLIT",FACE,{"disambiguationData":[TD([subQ6])],"derivedFrom":makeQuery(id+"FKiHbmxaIrGreLf_1.7.F3.boolean.opBoolean","SPLIT",FACE,{"disambiguationData":[TD([subQ6])],"derivedFrom":makeQuery(id+"FKiHbmxaIrGreLf_1.6.F3.boolean.opBoolean","SPLIT",FACE,{"disambiguationData":[TD([subQ6])],"derivedFrom":makeQuery(id+"FKiHbmxaIrGreLf_1.5.F3.boolean.opBoolean","SPLIT",FACE,{"disambiguationData":[TD([subQ6])],"derivedFrom":makeQuery(id+"FKiHbmxaIrGreLf_1.4.F3.boolean.opBoolean","SPLIT",FACE,{"disambiguationData":[TD([subQ6])],"derivedFrom":makeQuery(id+"FKiHbmxaIrGreLf_1.3.F3.boolean.opBoolean","SPLIT",FACE,{"disambiguationData":[TD([subQ6])],"derivedFrom":makeQuery(id+"FKiHbmxaIrGreLf_1.2.F3.boolean.opBoolean","SPLIT",FACE,{"disambiguationData":[TD([subQ6])],"derivedFrom":makeQuery(id+"FKiHbmxaIrGreLf_1.1.F3.boolean.opBoolean","SPLIT",FACE,{"disambiguationData":[TD([subQ6])],"derivedFrom":makeQuery(id+"F1.opRevolve","SWEPT_FACE",FACE,{"disambiguationData":[OSD([sQuery(id+"F0.wireOp",EDGE,"E2")])]})})})})})})})})})})})})})}),makeQuery(id+"FKiHbmxaIrGreLf_1.14.F3.opRevolve","CAP_FACE",FACE,{"disambiguationData":[OSD([subQ3,subQ2,subQ1,subQ0])],"isStart":false})]});}
            var Q12;
            {var subQ0=sQuery(id+"F2.wireOp",EDGE,"E13");var subQ1=sQuery(id+"F2.wireOp",EDGE,"E12");var subQ2=sQuery(id+"F2.wireOp",EDGE,"E11");var subQ3=sQuery(id+"F2.wireOp",EDGE,"E10");var subQ6=makeQuery(id+"F3.boolean.opBoolean","COPY",FACE,{"derivedFrom":makeQuery(id+"F3.opRevolve","CAP_FACE",FACE,{"disambiguationData":[OSD([subQ3,subQ2,subQ1,subQ0])],"isStart":true})});Q12=makeQuery(id+"FKiHbmxaIrGreLf_1.14.F3.boolean.opBoolean","INTERSECT",EDGE,{"derivedFrom":[makeQuery(id+"FKiHbmxaIrGreLf_1.13.F3.boolean.opBoolean","SPLIT",FACE,{"disambiguationData":[TD([subQ6])],"derivedFrom":makeQuery(id+"FKiHbmxaIrGreLf_1.12.F3.boolean.opBoolean","SPLIT",FACE,{"disambiguationData":[TD([subQ6])],"derivedFrom":makeQuery(id+"FKiHbmxaIrGreLf_1.11.F3.boolean.opBoolean","SPLIT",FACE,{"disambiguationData":[TD([subQ6])],"derivedFrom":makeQuery(id+"FKiHbmxaIrGreLf_1.10.F3.boolean.opBoolean","SPLIT",FACE,{"disambiguationData":[TD([subQ6])],"derivedFrom":makeQuery(id+"FKiHbmxaIrGreLf_1.9.F3.boolean.opBoolean","SPLIT",FACE,{"disambiguationData":[TD([subQ6])],"derivedFrom":makeQuery(id+"FKiHbmxaIrGreLf_1.8.F3.boolean.opBoolean","SPLIT",FACE,{"disambiguationData":[TD([subQ6])],"derivedFrom":makeQuery(id+"FKiHbmxaIrGreLf_1.7.F3.boolean.opBoolean","SPLIT",FACE,{"disambiguationData":[TD([subQ6])],"derivedFrom":makeQuery(id+"FKiHbmxaIrGreLf_1.6.F3.boolean.opBoolean","SPLIT",FACE,{"disambiguationData":[TD([subQ6])],"derivedFrom":makeQuery(id+"FKiHbmxaIrGreLf_1.5.F3.boolean.opBoolean","SPLIT",FACE,{"disambiguationData":[TD([subQ6])],"derivedFrom":makeQuery(id+"FKiHbmxaIrGreLf_1.4.F3.boolean.opBoolean","SPLIT",FACE,{"disambiguationData":[TD([subQ6])],"derivedFrom":makeQuery(id+"FKiHbmxaIrGreLf_1.3.F3.boolean.opBoolean","SPLIT",FACE,{"disambiguationData":[TD([subQ6])],"derivedFrom":makeQuery(id+"FKiHbmxaIrGreLf_1.2.F3.boolean.opBoolean","SPLIT",FACE,{"disambiguationData":[TD([subQ6])],"derivedFrom":makeQuery(id+"FKiHbmxaIrGreLf_1.1.F3.boolean.opBoolean","SPLIT",FACE,{"disambiguationData":[TD([subQ6])],"derivedFrom":makeQuery(id+"F1.opRevolve","SWEPT_FACE",FACE,{"disambiguationData":[OSD([sQuery(id+"F0.wireOp",EDGE,"E2")])]})})})})})})})})})})})})})}),makeQuery(id+"FKiHbmxaIrGreLf_1.14.F3.opRevolve","CAP_FACE",FACE,{"disambiguationData":[OSD([subQ3,subQ2,subQ1,subQ0])],"isStart":true})]});}
            var Q13;
            {var subQ0=sQuery(id+"F2.wireOp",EDGE,"E13");var subQ1=sQuery(id+"F2.wireOp",EDGE,"E12");var subQ2=sQuery(id+"F2.wireOp",EDGE,"E11");var subQ3=sQuery(id+"F2.wireOp",EDGE,"E10");var subQ6=makeQuery(id+"F3.boolean.opBoolean","COPY",FACE,{"derivedFrom":makeQuery(id+"F3.opRevolve","CAP_FACE",FACE,{"disambiguationData":[OSD([subQ3,subQ2,subQ1,subQ0])],"isStart":true})});Q13=makeQuery(id+"FKiHbmxaIrGreLf_1.13.F3.boolean.opBoolean","INTERSECT",EDGE,{"derivedFrom":[makeQuery(id+"FKiHbmxaIrGreLf_1.12.F3.boolean.opBoolean","SPLIT",FACE,{"disambiguationData":[TD([subQ6])],"derivedFrom":makeQuery(id+"FKiHbmxaIrGreLf_1.11.F3.boolean.opBoolean","SPLIT",FACE,{"disambiguationData":[TD([subQ6])],"derivedFrom":makeQuery(id+"FKiHbmxaIrGreLf_1.10.F3.boolean.opBoolean","SPLIT",FACE,{"disambiguationData":[TD([subQ6])],"derivedFrom":makeQuery(id+"FKiHbmxaIrGreLf_1.9.F3.boolean.opBoolean","SPLIT",FACE,{"disambiguationData":[TD([subQ6])],"derivedFrom":makeQuery(id+"FKiHbmxaIrGreLf_1.8.F3.boolean.opBoolean","SPLIT",FACE,{"disambiguationData":[TD([subQ6])],"derivedFrom":makeQuery(id+"FKiHbmxaIrGreLf_1.7.F3.boolean.opBoolean","SPLIT",FACE,{"disambiguationData":[TD([subQ6])],"derivedFrom":makeQuery(id+"FKiHbmxaIrGreLf_1.6.F3.boolean.opBoolean","SPLIT",FACE,{"disambiguationData":[TD([subQ6])],"derivedFrom":makeQuery(id+"FKiHbmxaIrGreLf_1.5.F3.boolean.opBoolean","SPLIT",FACE,{"disambiguationData":[TD([subQ6])],"derivedFrom":makeQuery(id+"FKiHbmxaIrGreLf_1.4.F3.boolean.opBoolean","SPLIT",FACE,{"disambiguationData":[TD([subQ6])],"derivedFrom":makeQuery(id+"FKiHbmxaIrGreLf_1.3.F3.boolean.opBoolean","SPLIT",FACE,{"disambiguationData":[TD([subQ6])],"derivedFrom":makeQuery(id+"FKiHbmxaIrGreLf_1.2.F3.boolean.opBoolean","SPLIT",FACE,{"disambiguationData":[TD([subQ6])],"derivedFrom":makeQuery(id+"FKiHbmxaIrGreLf_1.1.F3.boolean.opBoolean","SPLIT",FACE,{"disambiguationData":[TD([subQ6])],"derivedFrom":makeQuery(id+"F1.opRevolve","SWEPT_FACE",FACE,{"disambiguationData":[OSD([sQuery(id+"F0.wireOp",EDGE,"E2")])]})})})})})})})})})})})})}),makeQuery(id+"FKiHbmxaIrGreLf_1.13.F3.opRevolve","CAP_FACE",FACE,{"disambiguationData":[OSD([subQ3,subQ2,subQ1,subQ0])],"isStart":false})]});}
            var Q14;
            {var subQ0=sQuery(id+"F2.wireOp",EDGE,"E13");var subQ1=sQuery(id+"F2.wireOp",EDGE,"E12");var subQ2=sQuery(id+"F2.wireOp",EDGE,"E11");var subQ3=sQuery(id+"F2.wireOp",EDGE,"E10");var subQ6=makeQuery(id+"F3.boolean.opBoolean","COPY",FACE,{"derivedFrom":makeQuery(id+"F3.opRevolve","CAP_FACE",FACE,{"disambiguationData":[OSD([subQ3,subQ2,subQ1,subQ0])],"isStart":true})});Q14=makeQuery(id+"FKiHbmxaIrGreLf_1.13.F3.boolean.opBoolean","INTERSECT",EDGE,{"derivedFrom":[makeQuery(id+"FKiHbmxaIrGreLf_1.12.F3.boolean.opBoolean","SPLIT",FACE,{"disambiguationData":[TD([subQ6])],"derivedFrom":makeQuery(id+"FKiHbmxaIrGreLf_1.11.F3.boolean.opBoolean","SPLIT",FACE,{"disambiguationData":[TD([subQ6])],"derivedFrom":makeQuery(id+"FKiHbmxaIrGreLf_1.10.F3.boolean.opBoolean","SPLIT",FACE,{"disambiguationData":[TD([subQ6])],"derivedFrom":makeQuery(id+"FKiHbmxaIrGreLf_1.9.F3.boolean.opBoolean","SPLIT",FACE,{"disambiguationData":[TD([subQ6])],"derivedFrom":makeQuery(id+"FKiHbmxaIrGreLf_1.8.F3.boolean.opBoolean","SPLIT",FACE,{"disambiguationData":[TD([subQ6])],"derivedFrom":makeQuery(id+"FKiHbmxaIrGreLf_1.7.F3.boolean.opBoolean","SPLIT",FACE,{"disambiguationData":[TD([subQ6])],"derivedFrom":makeQuery(id+"FKiHbmxaIrGreLf_1.6.F3.boolean.opBoolean","SPLIT",FACE,{"disambiguationData":[TD([subQ6])],"derivedFrom":makeQuery(id+"FKiHbmxaIrGreLf_1.5.F3.boolean.opBoolean","SPLIT",FACE,{"disambiguationData":[TD([subQ6])],"derivedFrom":makeQuery(id+"FKiHbmxaIrGreLf_1.4.F3.boolean.opBoolean","SPLIT",FACE,{"disambiguationData":[TD([subQ6])],"derivedFrom":makeQuery(id+"FKiHbmxaIrGreLf_1.3.F3.boolean.opBoolean","SPLIT",FACE,{"disambiguationData":[TD([subQ6])],"derivedFrom":makeQuery(id+"FKiHbmxaIrGreLf_1.2.F3.boolean.opBoolean","SPLIT",FACE,{"disambiguationData":[TD([subQ6])],"derivedFrom":makeQuery(id+"FKiHbmxaIrGreLf_1.1.F3.boolean.opBoolean","SPLIT",FACE,{"disambiguationData":[TD([subQ6])],"derivedFrom":makeQuery(id+"F1.opRevolve","SWEPT_FACE",FACE,{"disambiguationData":[OSD([sQuery(id+"F0.wireOp",EDGE,"E2")])]})})})})})})})})})})})})}),makeQuery(id+"FKiHbmxaIrGreLf_1.13.F3.opRevolve","CAP_FACE",FACE,{"disambiguationData":[OSD([subQ3,subQ2,subQ1,subQ0])],"isStart":true})]});}
            var Q15;
            {var subQ0=sQuery(id+"F2.wireOp",EDGE,"E13");var subQ1=sQuery(id+"F2.wireOp",EDGE,"E12");var subQ2=sQuery(id+"F2.wireOp",EDGE,"E11");var subQ3=sQuery(id+"F2.wireOp",EDGE,"E10");var subQ6=makeQuery(id+"F3.boolean.opBoolean","COPY",FACE,{"derivedFrom":makeQuery(id+"F3.opRevolve","CAP_FACE",FACE,{"disambiguationData":[OSD([subQ3,subQ2,subQ1,subQ0])],"isStart":true})});Q15=makeQuery(id+"FKiHbmxaIrGreLf_1.12.F3.boolean.opBoolean","INTERSECT",EDGE,{"derivedFrom":[makeQuery(id+"FKiHbmxaIrGreLf_1.11.F3.boolean.opBoolean","SPLIT",FACE,{"disambiguationData":[TD([subQ6])],"derivedFrom":makeQuery(id+"FKiHbmxaIrGreLf_1.10.F3.boolean.opBoolean","SPLIT",FACE,{"disambiguationData":[TD([subQ6])],"derivedFrom":makeQuery(id+"FKiHbmxaIrGreLf_1.9.F3.boolean.opBoolean","SPLIT",FACE,{"disambiguationData":[TD([subQ6])],"derivedFrom":makeQuery(id+"FKiHbmxaIrGreLf_1.8.F3.boolean.opBoolean","SPLIT",FACE,{"disambiguationData":[TD([subQ6])],"derivedFrom":makeQuery(id+"FKiHbmxaIrGreLf_1.7.F3.boolean.opBoolean","SPLIT",FACE,{"disambiguationData":[TD([subQ6])],"derivedFrom":makeQuery(id+"FKiHbmxaIrGreLf_1.6.F3.boolean.opBoolean","SPLIT",FACE,{"disambiguationData":[TD([subQ6])],"derivedFrom":makeQuery(id+"FKiHbmxaIrGreLf_1.5.F3.boolean.opBoolean","SPLIT",FACE,{"disambiguationData":[TD([subQ6])],"derivedFrom":makeQuery(id+"FKiHbmxaIrGreLf_1.4.F3.boolean.opBoolean","SPLIT",FACE,{"disambiguationData":[TD([subQ6])],"derivedFrom":makeQuery(id+"FKiHbmxaIrGreLf_1.3.F3.boolean.opBoolean","SPLIT",FACE,{"disambiguationData":[TD([subQ6])],"derivedFrom":makeQuery(id+"FKiHbmxaIrGreLf_1.2.F3.boolean.opBoolean","SPLIT",FACE,{"disambiguationData":[TD([subQ6])],"derivedFrom":makeQuery(id+"FKiHbmxaIrGreLf_1.1.F3.boolean.opBoolean","SPLIT",FACE,{"disambiguationData":[TD([subQ6])],"derivedFrom":makeQuery(id+"F1.opRevolve","SWEPT_FACE",FACE,{"disambiguationData":[OSD([sQuery(id+"F0.wireOp",EDGE,"E2")])]})})})})})})})})})})})}),makeQuery(id+"FKiHbmxaIrGreLf_1.12.F3.opRevolve","CAP_FACE",FACE,{"disambiguationData":[OSD([subQ3,subQ2,subQ1,subQ0])],"isStart":false})]});}
            var Q16;
            {var subQ0=sQuery(id+"F2.wireOp",EDGE,"E13");var subQ1=sQuery(id+"F2.wireOp",EDGE,"E12");var subQ2=sQuery(id+"F2.wireOp",EDGE,"E11");var subQ3=sQuery(id+"F2.wireOp",EDGE,"E10");var subQ6=makeQuery(id+"F3.boolean.opBoolean","COPY",FACE,{"derivedFrom":makeQuery(id+"F3.opRevolve","CAP_FACE",FACE,{"disambiguationData":[OSD([subQ3,subQ2,subQ1,subQ0])],"isStart":true})});Q16=makeQuery(id+"FKiHbmxaIrGreLf_1.12.F3.boolean.opBoolean","INTERSECT",EDGE,{"derivedFrom":[makeQuery(id+"FKiHbmxaIrGreLf_1.11.F3.boolean.opBoolean","SPLIT",FACE,{"disambiguationData":[TD([subQ6])],"derivedFrom":makeQuery(id+"FKiHbmxaIrGreLf_1.10.F3.boolean.opBoolean","SPLIT",FACE,{"disambiguationData":[TD([subQ6])],"derivedFrom":makeQuery(id+"FKiHbmxaIrGreLf_1.9.F3.boolean.opBoolean","SPLIT",FACE,{"disambiguationData":[TD([subQ6])],"derivedFrom":makeQuery(id+"FKiHbmxaIrGreLf_1.8.F3.boolean.opBoolean","SPLIT",FACE,{"disambiguationData":[TD([subQ6])],"derivedFrom":makeQuery(id+"FKiHbmxaIrGreLf_1.7.F3.boolean.opBoolean","SPLIT",FACE,{"disambiguationData":[TD([subQ6])],"derivedFrom":makeQuery(id+"FKiHbmxaIrGreLf_1.6.F3.boolean.opBoolean","SPLIT",FACE,{"disambiguationData":[TD([subQ6])],"derivedFrom":makeQuery(id+"FKiHbmxaIrGreLf_1.5.F3.boolean.opBoolean","SPLIT",FACE,{"disambiguationData":[TD([subQ6])],"derivedFrom":makeQuery(id+"FKiHbmxaIrGreLf_1.4.F3.boolean.opBoolean","SPLIT",FACE,{"disambiguationData":[TD([subQ6])],"derivedFrom":makeQuery(id+"FKiHbmxaIrGreLf_1.3.F3.boolean.opBoolean","SPLIT",FACE,{"disambiguationData":[TD([subQ6])],"derivedFrom":makeQuery(id+"FKiHbmxaIrGreLf_1.2.F3.boolean.opBoolean","SPLIT",FACE,{"disambiguationData":[TD([subQ6])],"derivedFrom":makeQuery(id+"FKiHbmxaIrGreLf_1.1.F3.boolean.opBoolean","SPLIT",FACE,{"disambiguationData":[TD([subQ6])],"derivedFrom":makeQuery(id+"F1.opRevolve","SWEPT_FACE",FACE,{"disambiguationData":[OSD([sQuery(id+"F0.wireOp",EDGE,"E2")])]})})})})})})})})})})})}),makeQuery(id+"FKiHbmxaIrGreLf_1.12.F3.opRevolve","CAP_FACE",FACE,{"disambiguationData":[OSD([subQ3,subQ2,subQ1,subQ0])],"isStart":true})]});}
            var Q17;
            {var subQ0=sQuery(id+"F2.wireOp",EDGE,"E13");var subQ1=sQuery(id+"F2.wireOp",EDGE,"E12");var subQ2=sQuery(id+"F2.wireOp",EDGE,"E11");var subQ3=sQuery(id+"F2.wireOp",EDGE,"E10");var subQ6=makeQuery(id+"F3.boolean.opBoolean","COPY",FACE,{"derivedFrom":makeQuery(id+"F3.opRevolve","CAP_FACE",FACE,{"disambiguationData":[OSD([subQ3,subQ2,subQ1,subQ0])],"isStart":true})});Q17=makeQuery(id+"FKiHbmxaIrGreLf_1.11.F3.boolean.opBoolean","INTERSECT",EDGE,{"derivedFrom":[makeQuery(id+"FKiHbmxaIrGreLf_1.10.F3.boolean.opBoolean","SPLIT",FACE,{"disambiguationData":[TD([subQ6])],"derivedFrom":makeQuery(id+"FKiHbmxaIrGreLf_1.9.F3.boolean.opBoolean","SPLIT",FACE,{"disambiguationData":[TD([subQ6])],"derivedFrom":makeQuery(id+"FKiHbmxaIrGreLf_1.8.F3.boolean.opBoolean","SPLIT",FACE,{"disambiguationData":[TD([subQ6])],"derivedFrom":makeQuery(id+"FKiHbmxaIrGreLf_1.7.F3.boolean.opBoolean","SPLIT",FACE,{"disambiguationData":[TD([subQ6])],"derivedFrom":makeQuery(id+"FKiHbmxaIrGreLf_1.6.F3.boolean.opBoolean","SPLIT",FACE,{"disambiguationData":[TD([subQ6])],"derivedFrom":makeQuery(id+"FKiHbmxaIrGreLf_1.5.F3.boolean.opBoolean","SPLIT",FACE,{"disambiguationData":[TD([subQ6])],"derivedFrom":makeQuery(id+"FKiHbmxaIrGreLf_1.4.F3.boolean.opBoolean","SPLIT",FACE,{"disambiguationData":[TD([subQ6])],"derivedFrom":makeQuery(id+"FKiHbmxaIrGreLf_1.3.F3.boolean.opBoolean","SPLIT",FACE,{"disambiguationData":[TD([subQ6])],"derivedFrom":makeQuery(id+"FKiHbmxaIrGreLf_1.2.F3.boolean.opBoolean","SPLIT",FACE,{"disambiguationData":[TD([subQ6])],"derivedFrom":makeQuery(id+"FKiHbmxaIrGreLf_1.1.F3.boolean.opBoolean","SPLIT",FACE,{"disambiguationData":[TD([subQ6])],"derivedFrom":makeQuery(id+"F1.opRevolve","SWEPT_FACE",FACE,{"disambiguationData":[OSD([sQuery(id+"F0.wireOp",EDGE,"E2")])]})})})})})})})})})})}),makeQuery(id+"FKiHbmxaIrGreLf_1.11.F3.opRevolve","CAP_FACE",FACE,{"disambiguationData":[OSD([subQ3,subQ2,subQ1,subQ0])],"isStart":false})]});}
            var Q18;
            {var subQ0=sQuery(id+"F2.wireOp",EDGE,"E13");var subQ1=sQuery(id+"F2.wireOp",EDGE,"E12");var subQ2=sQuery(id+"F2.wireOp",EDGE,"E11");var subQ3=sQuery(id+"F2.wireOp",EDGE,"E10");var subQ6=makeQuery(id+"F3.boolean.opBoolean","COPY",FACE,{"derivedFrom":makeQuery(id+"F3.opRevolve","CAP_FACE",FACE,{"disambiguationData":[OSD([subQ3,subQ2,subQ1,subQ0])],"isStart":true})});Q18=makeQuery(id+"FKiHbmxaIrGreLf_1.11.F3.boolean.opBoolean","INTERSECT",EDGE,{"derivedFrom":[makeQuery(id+"FKiHbmxaIrGreLf_1.10.F3.boolean.opBoolean","SPLIT",FACE,{"disambiguationData":[TD([subQ6])],"derivedFrom":makeQuery(id+"FKiHbmxaIrGreLf_1.9.F3.boolean.opBoolean","SPLIT",FACE,{"disambiguationData":[TD([subQ6])],"derivedFrom":makeQuery(id+"FKiHbmxaIrGreLf_1.8.F3.boolean.opBoolean","SPLIT",FACE,{"disambiguationData":[TD([subQ6])],"derivedFrom":makeQuery(id+"FKiHbmxaIrGreLf_1.7.F3.boolean.opBoolean","SPLIT",FACE,{"disambiguationData":[TD([subQ6])],"derivedFrom":makeQuery(id+"FKiHbmxaIrGreLf_1.6.F3.boolean.opBoolean","SPLIT",FACE,{"disambiguationData":[TD([subQ6])],"derivedFrom":makeQuery(id+"FKiHbmxaIrGreLf_1.5.F3.boolean.opBoolean","SPLIT",FACE,{"disambiguationData":[TD([subQ6])],"derivedFrom":makeQuery(id+"FKiHbmxaIrGreLf_1.4.F3.boolean.opBoolean","SPLIT",FACE,{"disambiguationData":[TD([subQ6])],"derivedFrom":makeQuery(id+"FKiHbmxaIrGreLf_1.3.F3.boolean.opBoolean","SPLIT",FACE,{"disambiguationData":[TD([subQ6])],"derivedFrom":makeQuery(id+"FKiHbmxaIrGreLf_1.2.F3.boolean.opBoolean","SPLIT",FACE,{"disambiguationData":[TD([subQ6])],"derivedFrom":makeQuery(id+"FKiHbmxaIrGreLf_1.1.F3.boolean.opBoolean","SPLIT",FACE,{"disambiguationData":[TD([subQ6])],"derivedFrom":makeQuery(id+"F1.opRevolve","SWEPT_FACE",FACE,{"disambiguationData":[OSD([sQuery(id+"F0.wireOp",EDGE,"E2")])]})})})})})})})})})})}),makeQuery(id+"FKiHbmxaIrGreLf_1.11.F3.opRevolve","CAP_FACE",FACE,{"disambiguationData":[OSD([subQ3,subQ2,subQ1,subQ0])],"isStart":true})]});}
            var Q19;
            {var subQ0=sQuery(id+"F2.wireOp",EDGE,"E13");var subQ1=sQuery(id+"F2.wireOp",EDGE,"E12");var subQ2=sQuery(id+"F2.wireOp",EDGE,"E11");var subQ3=sQuery(id+"F2.wireOp",EDGE,"E10");var subQ6=makeQuery(id+"F3.boolean.opBoolean","COPY",FACE,{"derivedFrom":makeQuery(id+"F3.opRevolve","CAP_FACE",FACE,{"disambiguationData":[OSD([subQ3,subQ2,subQ1,subQ0])],"isStart":true})});Q19=makeQuery(id+"FKiHbmxaIrGreLf_1.10.F3.boolean.opBoolean","INTERSECT",EDGE,{"derivedFrom":[makeQuery(id+"FKiHbmxaIrGreLf_1.9.F3.boolean.opBoolean","SPLIT",FACE,{"disambiguationData":[TD([subQ6])],"derivedFrom":makeQuery(id+"FKiHbmxaIrGreLf_1.8.F3.boolean.opBoolean","SPLIT",FACE,{"disambiguationData":[TD([subQ6])],"derivedFrom":makeQuery(id+"FKiHbmxaIrGreLf_1.7.F3.boolean.opBoolean","SPLIT",FACE,{"disambiguationData":[TD([subQ6])],"derivedFrom":makeQuery(id+"FKiHbmxaIrGreLf_1.6.F3.boolean.opBoolean","SPLIT",FACE,{"disambiguationData":[TD([subQ6])],"derivedFrom":makeQuery(id+"FKiHbmxaIrGreLf_1.5.F3.boolean.opBoolean","SPLIT",FACE,{"disambiguationData":[TD([subQ6])],"derivedFrom":makeQuery(id+"FKiHbmxaIrGreLf_1.4.F3.boolean.opBoolean","SPLIT",FACE,{"disambiguationData":[TD([subQ6])],"derivedFrom":makeQuery(id+"FKiHbmxaIrGreLf_1.3.F3.boolean.opBoolean","SPLIT",FACE,{"disambiguationData":[TD([subQ6])],"derivedFrom":makeQuery(id+"FKiHbmxaIrGreLf_1.2.F3.boolean.opBoolean","SPLIT",FACE,{"disambiguationData":[TD([subQ6])],"derivedFrom":makeQuery(id+"FKiHbmxaIrGreLf_1.1.F3.boolean.opBoolean","SPLIT",FACE,{"disambiguationData":[TD([subQ6])],"derivedFrom":makeQuery(id+"F1.opRevolve","SWEPT_FACE",FACE,{"disambiguationData":[OSD([sQuery(id+"F0.wireOp",EDGE,"E2")])]})})})})})})})})})}),makeQuery(id+"FKiHbmxaIrGreLf_1.10.F3.opRevolve","CAP_FACE",FACE,{"disambiguationData":[OSD([subQ3,subQ2,subQ1,subQ0])],"isStart":false})]});}
            var Q20;
            {var subQ0=sQuery(id+"F2.wireOp",EDGE,"E13");var subQ1=sQuery(id+"F2.wireOp",EDGE,"E12");var subQ2=sQuery(id+"F2.wireOp",EDGE,"E11");var subQ3=sQuery(id+"F2.wireOp",EDGE,"E10");var subQ6=makeQuery(id+"F3.boolean.opBoolean","COPY",FACE,{"derivedFrom":makeQuery(id+"F3.opRevolve","CAP_FACE",FACE,{"disambiguationData":[OSD([subQ3,subQ2,subQ1,subQ0])],"isStart":true})});Q20=makeQuery(id+"FKiHbmxaIrGreLf_1.10.F3.boolean.opBoolean","INTERSECT",EDGE,{"derivedFrom":[makeQuery(id+"FKiHbmxaIrGreLf_1.9.F3.boolean.opBoolean","SPLIT",FACE,{"disambiguationData":[TD([subQ6])],"derivedFrom":makeQuery(id+"FKiHbmxaIrGreLf_1.8.F3.boolean.opBoolean","SPLIT",FACE,{"disambiguationData":[TD([subQ6])],"derivedFrom":makeQuery(id+"FKiHbmxaIrGreLf_1.7.F3.boolean.opBoolean","SPLIT",FACE,{"disambiguationData":[TD([subQ6])],"derivedFrom":makeQuery(id+"FKiHbmxaIrGreLf_1.6.F3.boolean.opBoolean","SPLIT",FACE,{"disambiguationData":[TD([subQ6])],"derivedFrom":makeQuery(id+"FKiHbmxaIrGreLf_1.5.F3.boolean.opBoolean","SPLIT",FACE,{"disambiguationData":[TD([subQ6])],"derivedFrom":makeQuery(id+"FKiHbmxaIrGreLf_1.4.F3.boolean.opBoolean","SPLIT",FACE,{"disambiguationData":[TD([subQ6])],"derivedFrom":makeQuery(id+"FKiHbmxaIrGreLf_1.3.F3.boolean.opBoolean","SPLIT",FACE,{"disambiguationData":[TD([subQ6])],"derivedFrom":makeQuery(id+"FKiHbmxaIrGreLf_1.2.F3.boolean.opBoolean","SPLIT",FACE,{"disambiguationData":[TD([subQ6])],"derivedFrom":makeQuery(id+"FKiHbmxaIrGreLf_1.1.F3.boolean.opBoolean","SPLIT",FACE,{"disambiguationData":[TD([subQ6])],"derivedFrom":makeQuery(id+"F1.opRevolve","SWEPT_FACE",FACE,{"disambiguationData":[OSD([sQuery(id+"F0.wireOp",EDGE,"E2")])]})})})})})})})})})}),makeQuery(id+"FKiHbmxaIrGreLf_1.10.F3.opRevolve","CAP_FACE",FACE,{"disambiguationData":[OSD([subQ3,subQ2,subQ1,subQ0])],"isStart":true})]});}
            var Q21;
            {var subQ0=sQuery(id+"F2.wireOp",EDGE,"E13");var subQ1=sQuery(id+"F2.wireOp",EDGE,"E12");var subQ2=sQuery(id+"F2.wireOp",EDGE,"E11");var subQ3=sQuery(id+"F2.wireOp",EDGE,"E10");var subQ6=makeQuery(id+"F3.boolean.opBoolean","COPY",FACE,{"derivedFrom":makeQuery(id+"F3.opRevolve","CAP_FACE",FACE,{"disambiguationData":[OSD([subQ3,subQ2,subQ1,subQ0])],"isStart":true})});Q21=makeQuery(id+"FKiHbmxaIrGreLf_1.9.F3.boolean.opBoolean","INTERSECT",EDGE,{"derivedFrom":[makeQuery(id+"FKiHbmxaIrGreLf_1.8.F3.boolean.opBoolean","SPLIT",FACE,{"disambiguationData":[TD([subQ6])],"derivedFrom":makeQuery(id+"FKiHbmxaIrGreLf_1.7.F3.boolean.opBoolean","SPLIT",FACE,{"disambiguationData":[TD([subQ6])],"derivedFrom":makeQuery(id+"FKiHbmxaIrGreLf_1.6.F3.boolean.opBoolean","SPLIT",FACE,{"disambiguationData":[TD([subQ6])],"derivedFrom":makeQuery(id+"FKiHbmxaIrGreLf_1.5.F3.boolean.opBoolean","SPLIT",FACE,{"disambiguationData":[TD([subQ6])],"derivedFrom":makeQuery(id+"FKiHbmxaIrGreLf_1.4.F3.boolean.opBoolean","SPLIT",FACE,{"disambiguationData":[TD([subQ6])],"derivedFrom":makeQuery(id+"FKiHbmxaIrGreLf_1.3.F3.boolean.opBoolean","SPLIT",FACE,{"disambiguationData":[TD([subQ6])],"derivedFrom":makeQuery(id+"FKiHbmxaIrGreLf_1.2.F3.boolean.opBoolean","SPLIT",FACE,{"disambiguationData":[TD([subQ6])],"derivedFrom":makeQuery(id+"FKiHbmxaIrGreLf_1.1.F3.boolean.opBoolean","SPLIT",FACE,{"disambiguationData":[TD([subQ6])],"derivedFrom":makeQuery(id+"F1.opRevolve","SWEPT_FACE",FACE,{"disambiguationData":[OSD([sQuery(id+"F0.wireOp",EDGE,"E2")])]})})})})})})})})}),makeQuery(id+"FKiHbmxaIrGreLf_1.9.F3.opRevolve","CAP_FACE",FACE,{"disambiguationData":[OSD([subQ3,subQ2,subQ1,subQ0])],"isStart":false})]});}
            var Q22;
            {var subQ0=sQuery(id+"F2.wireOp",EDGE,"E13");var subQ1=sQuery(id+"F2.wireOp",EDGE,"E12");var subQ2=sQuery(id+"F2.wireOp",EDGE,"E11");var subQ3=sQuery(id+"F2.wireOp",EDGE,"E10");var subQ6=makeQuery(id+"F3.boolean.opBoolean","COPY",FACE,{"derivedFrom":makeQuery(id+"F3.opRevolve","CAP_FACE",FACE,{"disambiguationData":[OSD([subQ3,subQ2,subQ1,subQ0])],"isStart":true})});Q22=makeQuery(id+"FKiHbmxaIrGreLf_1.9.F3.boolean.opBoolean","INTERSECT",EDGE,{"derivedFrom":[makeQuery(id+"FKiHbmxaIrGreLf_1.8.F3.boolean.opBoolean","SPLIT",FACE,{"disambiguationData":[TD([subQ6])],"derivedFrom":makeQuery(id+"FKiHbmxaIrGreLf_1.7.F3.boolean.opBoolean","SPLIT",FACE,{"disambiguationData":[TD([subQ6])],"derivedFrom":makeQuery(id+"FKiHbmxaIrGreLf_1.6.F3.boolean.opBoolean","SPLIT",FACE,{"disambiguationData":[TD([subQ6])],"derivedFrom":makeQuery(id+"FKiHbmxaIrGreLf_1.5.F3.boolean.opBoolean","SPLIT",FACE,{"disambiguationData":[TD([subQ6])],"derivedFrom":makeQuery(id+"FKiHbmxaIrGreLf_1.4.F3.boolean.opBoolean","SPLIT",FACE,{"disambiguationData":[TD([subQ6])],"derivedFrom":makeQuery(id+"FKiHbmxaIrGreLf_1.3.F3.boolean.opBoolean","SPLIT",FACE,{"disambiguationData":[TD([subQ6])],"derivedFrom":makeQuery(id+"FKiHbmxaIrGreLf_1.2.F3.boolean.opBoolean","SPLIT",FACE,{"disambiguationData":[TD([subQ6])],"derivedFrom":makeQuery(id+"FKiHbmxaIrGreLf_1.1.F3.boolean.opBoolean","SPLIT",FACE,{"disambiguationData":[TD([subQ6])],"derivedFrom":makeQuery(id+"F1.opRevolve","SWEPT_FACE",FACE,{"disambiguationData":[OSD([sQuery(id+"F0.wireOp",EDGE,"E2")])]})})})})})})})})}),makeQuery(id+"FKiHbmxaIrGreLf_1.9.F3.opRevolve","CAP_FACE",FACE,{"disambiguationData":[OSD([subQ3,subQ2,subQ1,subQ0])],"isStart":true})]});}
            var Q23;
            {var subQ0=sQuery(id+"F2.wireOp",EDGE,"E13");var subQ1=sQuery(id+"F2.wireOp",EDGE,"E12");var subQ2=sQuery(id+"F2.wireOp",EDGE,"E11");var subQ3=sQuery(id+"F2.wireOp",EDGE,"E10");var subQ6=makeQuery(id+"F3.boolean.opBoolean","COPY",FACE,{"derivedFrom":makeQuery(id+"F3.opRevolve","CAP_FACE",FACE,{"disambiguationData":[OSD([subQ3,subQ2,subQ1,subQ0])],"isStart":true})});Q23=makeQuery(id+"FKiHbmxaIrGreLf_1.8.F3.boolean.opBoolean","INTERSECT",EDGE,{"derivedFrom":[makeQuery(id+"FKiHbmxaIrGreLf_1.7.F3.boolean.opBoolean","SPLIT",FACE,{"disambiguationData":[TD([subQ6])],"derivedFrom":makeQuery(id+"FKiHbmxaIrGreLf_1.6.F3.boolean.opBoolean","SPLIT",FACE,{"disambiguationData":[TD([subQ6])],"derivedFrom":makeQuery(id+"FKiHbmxaIrGreLf_1.5.F3.boolean.opBoolean","SPLIT",FACE,{"disambiguationData":[TD([subQ6])],"derivedFrom":makeQuery(id+"FKiHbmxaIrGreLf_1.4.F3.boolean.opBoolean","SPLIT",FACE,{"disambiguationData":[TD([subQ6])],"derivedFrom":makeQuery(id+"FKiHbmxaIrGreLf_1.3.F3.boolean.opBoolean","SPLIT",FACE,{"disambiguationData":[TD([subQ6])],"derivedFrom":makeQuery(id+"FKiHbmxaIrGreLf_1.2.F3.boolean.opBoolean","SPLIT",FACE,{"disambiguationData":[TD([subQ6])],"derivedFrom":makeQuery(id+"FKiHbmxaIrGreLf_1.1.F3.boolean.opBoolean","SPLIT",FACE,{"disambiguationData":[TD([subQ6])],"derivedFrom":makeQuery(id+"F1.opRevolve","SWEPT_FACE",FACE,{"disambiguationData":[OSD([sQuery(id+"F0.wireOp",EDGE,"E2")])]})})})})})})})}),makeQuery(id+"FKiHbmxaIrGreLf_1.8.F3.opRevolve","CAP_FACE",FACE,{"disambiguationData":[OSD([subQ3,subQ2,subQ1,subQ0])],"isStart":false})]});}
            var Q24;
            {var subQ0=sQuery(id+"F2.wireOp",EDGE,"E13");var subQ1=sQuery(id+"F2.wireOp",EDGE,"E12");var subQ2=sQuery(id+"F2.wireOp",EDGE,"E11");var subQ3=sQuery(id+"F2.wireOp",EDGE,"E10");var subQ6=makeQuery(id+"F3.boolean.opBoolean","COPY",FACE,{"derivedFrom":makeQuery(id+"F3.opRevolve","CAP_FACE",FACE,{"disambiguationData":[OSD([subQ3,subQ2,subQ1,subQ0])],"isStart":true})});Q24=makeQuery(id+"FKiHbmxaIrGreLf_1.8.F3.boolean.opBoolean","INTERSECT",EDGE,{"derivedFrom":[makeQuery(id+"FKiHbmxaIrGreLf_1.7.F3.boolean.opBoolean","SPLIT",FACE,{"disambiguationData":[TD([subQ6])],"derivedFrom":makeQuery(id+"FKiHbmxaIrGreLf_1.6.F3.boolean.opBoolean","SPLIT",FACE,{"disambiguationData":[TD([subQ6])],"derivedFrom":makeQuery(id+"FKiHbmxaIrGreLf_1.5.F3.boolean.opBoolean","SPLIT",FACE,{"disambiguationData":[TD([subQ6])],"derivedFrom":makeQuery(id+"FKiHbmxaIrGreLf_1.4.F3.boolean.opBoolean","SPLIT",FACE,{"disambiguationData":[TD([subQ6])],"derivedFrom":makeQuery(id+"FKiHbmxaIrGreLf_1.3.F3.boolean.opBoolean","SPLIT",FACE,{"disambiguationData":[TD([subQ6])],"derivedFrom":makeQuery(id+"FKiHbmxaIrGreLf_1.2.F3.boolean.opBoolean","SPLIT",FACE,{"disambiguationData":[TD([subQ6])],"derivedFrom":makeQuery(id+"FKiHbmxaIrGreLf_1.1.F3.boolean.opBoolean","SPLIT",FACE,{"disambiguationData":[TD([subQ6])],"derivedFrom":makeQuery(id+"F1.opRevolve","SWEPT_FACE",FACE,{"disambiguationData":[OSD([sQuery(id+"F0.wireOp",EDGE,"E2")])]})})})})})})})}),makeQuery(id+"FKiHbmxaIrGreLf_1.8.F3.opRevolve","CAP_FACE",FACE,{"disambiguationData":[OSD([subQ3,subQ2,subQ1,subQ0])],"isStart":true})]});}
            var Q25;
            {var subQ0=sQuery(id+"F2.wireOp",EDGE,"E13");var subQ1=sQuery(id+"F2.wireOp",EDGE,"E12");var subQ2=sQuery(id+"F2.wireOp",EDGE,"E11");var subQ3=sQuery(id+"F2.wireOp",EDGE,"E10");var subQ6=makeQuery(id+"F3.boolean.opBoolean","COPY",FACE,{"derivedFrom":makeQuery(id+"F3.opRevolve","CAP_FACE",FACE,{"disambiguationData":[OSD([subQ3,subQ2,subQ1,subQ0])],"isStart":true})});Q25=makeQuery(id+"FKiHbmxaIrGreLf_1.7.F3.boolean.opBoolean","INTERSECT",EDGE,{"derivedFrom":[makeQuery(id+"FKiHbmxaIrGreLf_1.6.F3.boolean.opBoolean","SPLIT",FACE,{"disambiguationData":[TD([subQ6])],"derivedFrom":makeQuery(id+"FKiHbmxaIrGreLf_1.5.F3.boolean.opBoolean","SPLIT",FACE,{"disambiguationData":[TD([subQ6])],"derivedFrom":makeQuery(id+"FKiHbmxaIrGreLf_1.4.F3.boolean.opBoolean","SPLIT",FACE,{"disambiguationData":[TD([subQ6])],"derivedFrom":makeQuery(id+"FKiHbmxaIrGreLf_1.3.F3.boolean.opBoolean","SPLIT",FACE,{"disambiguationData":[TD([subQ6])],"derivedFrom":makeQuery(id+"FKiHbmxaIrGreLf_1.2.F3.boolean.opBoolean","SPLIT",FACE,{"disambiguationData":[TD([subQ6])],"derivedFrom":makeQuery(id+"FKiHbmxaIrGreLf_1.1.F3.boolean.opBoolean","SPLIT",FACE,{"disambiguationData":[TD([subQ6])],"derivedFrom":makeQuery(id+"F1.opRevolve","SWEPT_FACE",FACE,{"disambiguationData":[OSD([sQuery(id+"F0.wireOp",EDGE,"E2")])]})})})})})})}),makeQuery(id+"FKiHbmxaIrGreLf_1.7.F3.opRevolve","CAP_FACE",FACE,{"disambiguationData":[OSD([subQ3,subQ2,subQ1,subQ0])],"isStart":false})]});}
            var Q26;
            {var subQ0=sQuery(id+"F2.wireOp",EDGE,"E13");var subQ1=sQuery(id+"F2.wireOp",EDGE,"E12");var subQ2=sQuery(id+"F2.wireOp",EDGE,"E11");var subQ3=sQuery(id+"F2.wireOp",EDGE,"E10");var subQ6=makeQuery(id+"F3.boolean.opBoolean","COPY",FACE,{"derivedFrom":makeQuery(id+"F3.opRevolve","CAP_FACE",FACE,{"disambiguationData":[OSD([subQ3,subQ2,subQ1,subQ0])],"isStart":true})});Q26=makeQuery(id+"FKiHbmxaIrGreLf_1.7.F3.boolean.opBoolean","INTERSECT",EDGE,{"derivedFrom":[makeQuery(id+"FKiHbmxaIrGreLf_1.6.F3.boolean.opBoolean","SPLIT",FACE,{"disambiguationData":[TD([subQ6])],"derivedFrom":makeQuery(id+"FKiHbmxaIrGreLf_1.5.F3.boolean.opBoolean","SPLIT",FACE,{"disambiguationData":[TD([subQ6])],"derivedFrom":makeQuery(id+"FKiHbmxaIrGreLf_1.4.F3.boolean.opBoolean","SPLIT",FACE,{"disambiguationData":[TD([subQ6])],"derivedFrom":makeQuery(id+"FKiHbmxaIrGreLf_1.3.F3.boolean.opBoolean","SPLIT",FACE,{"disambiguationData":[TD([subQ6])],"derivedFrom":makeQuery(id+"FKiHbmxaIrGreLf_1.2.F3.boolean.opBoolean","SPLIT",FACE,{"disambiguationData":[TD([subQ6])],"derivedFrom":makeQuery(id+"FKiHbmxaIrGreLf_1.1.F3.boolean.opBoolean","SPLIT",FACE,{"disambiguationData":[TD([subQ6])],"derivedFrom":makeQuery(id+"F1.opRevolve","SWEPT_FACE",FACE,{"disambiguationData":[OSD([sQuery(id+"F0.wireOp",EDGE,"E2")])]})})})})})})}),makeQuery(id+"FKiHbmxaIrGreLf_1.7.F3.opRevolve","CAP_FACE",FACE,{"disambiguationData":[OSD([subQ3,subQ2,subQ1,subQ0])],"isStart":true})]});}
            var Q27;
            {var subQ0=sQuery(id+"F2.wireOp",EDGE,"E13");var subQ1=sQuery(id+"F2.wireOp",EDGE,"E12");var subQ2=sQuery(id+"F2.wireOp",EDGE,"E11");var subQ3=sQuery(id+"F2.wireOp",EDGE,"E10");var subQ6=makeQuery(id+"F3.boolean.opBoolean","COPY",FACE,{"derivedFrom":makeQuery(id+"F3.opRevolve","CAP_FACE",FACE,{"disambiguationData":[OSD([subQ3,subQ2,subQ1,subQ0])],"isStart":true})});Q27=makeQuery(id+"FKiHbmxaIrGreLf_1.6.F3.boolean.opBoolean","INTERSECT",EDGE,{"derivedFrom":[makeQuery(id+"FKiHbmxaIrGreLf_1.5.F3.boolean.opBoolean","SPLIT",FACE,{"disambiguationData":[TD([subQ6])],"derivedFrom":makeQuery(id+"FKiHbmxaIrGreLf_1.4.F3.boolean.opBoolean","SPLIT",FACE,{"disambiguationData":[TD([subQ6])],"derivedFrom":makeQuery(id+"FKiHbmxaIrGreLf_1.3.F3.boolean.opBoolean","SPLIT",FACE,{"disambiguationData":[TD([subQ6])],"derivedFrom":makeQuery(id+"FKiHbmxaIrGreLf_1.2.F3.boolean.opBoolean","SPLIT",FACE,{"disambiguationData":[TD([subQ6])],"derivedFrom":makeQuery(id+"FKiHbmxaIrGreLf_1.1.F3.boolean.opBoolean","SPLIT",FACE,{"disambiguationData":[TD([subQ6])],"derivedFrom":makeQuery(id+"F1.opRevolve","SWEPT_FACE",FACE,{"disambiguationData":[OSD([sQuery(id+"F0.wireOp",EDGE,"E2")])]})})})})})}),makeQuery(id+"FKiHbmxaIrGreLf_1.6.F3.opRevolve","CAP_FACE",FACE,{"disambiguationData":[OSD([subQ3,subQ2,subQ1,subQ0])],"isStart":false})]});}
            var Q28;
            {var subQ0=sQuery(id+"F2.wireOp",EDGE,"E13");var subQ1=sQuery(id+"F2.wireOp",EDGE,"E12");var subQ2=sQuery(id+"F2.wireOp",EDGE,"E11");var subQ3=sQuery(id+"F2.wireOp",EDGE,"E10");var subQ6=makeQuery(id+"F3.boolean.opBoolean","COPY",FACE,{"derivedFrom":makeQuery(id+"F3.opRevolve","CAP_FACE",FACE,{"disambiguationData":[OSD([subQ3,subQ2,subQ1,subQ0])],"isStart":true})});Q28=makeQuery(id+"FKiHbmxaIrGreLf_1.6.F3.boolean.opBoolean","INTERSECT",EDGE,{"derivedFrom":[makeQuery(id+"FKiHbmxaIrGreLf_1.5.F3.boolean.opBoolean","SPLIT",FACE,{"disambiguationData":[TD([subQ6])],"derivedFrom":makeQuery(id+"FKiHbmxaIrGreLf_1.4.F3.boolean.opBoolean","SPLIT",FACE,{"disambiguationData":[TD([subQ6])],"derivedFrom":makeQuery(id+"FKiHbmxaIrGreLf_1.3.F3.boolean.opBoolean","SPLIT",FACE,{"disambiguationData":[TD([subQ6])],"derivedFrom":makeQuery(id+"FKiHbmxaIrGreLf_1.2.F3.boolean.opBoolean","SPLIT",FACE,{"disambiguationData":[TD([subQ6])],"derivedFrom":makeQuery(id+"FKiHbmxaIrGreLf_1.1.F3.boolean.opBoolean","SPLIT",FACE,{"disambiguationData":[TD([subQ6])],"derivedFrom":makeQuery(id+"F1.opRevolve","SWEPT_FACE",FACE,{"disambiguationData":[OSD([sQuery(id+"F0.wireOp",EDGE,"E2")])]})})})})})}),makeQuery(id+"FKiHbmxaIrGreLf_1.6.F3.opRevolve","CAP_FACE",FACE,{"disambiguationData":[OSD([subQ3,subQ2,subQ1,subQ0])],"isStart":true})]});}
            var Q29;
            {var subQ0=sQuery(id+"F2.wireOp",EDGE,"E13");var subQ1=sQuery(id+"F2.wireOp",EDGE,"E12");var subQ2=sQuery(id+"F2.wireOp",EDGE,"E11");var subQ3=sQuery(id+"F2.wireOp",EDGE,"E10");var subQ6=makeQuery(id+"F3.boolean.opBoolean","COPY",FACE,{"derivedFrom":makeQuery(id+"F3.opRevolve","CAP_FACE",FACE,{"disambiguationData":[OSD([subQ3,subQ2,subQ1,subQ0])],"isStart":true})});Q29=makeQuery(id+"FKiHbmxaIrGreLf_1.5.F3.boolean.opBoolean","INTERSECT",EDGE,{"derivedFrom":[makeQuery(id+"FKiHbmxaIrGreLf_1.4.F3.boolean.opBoolean","SPLIT",FACE,{"disambiguationData":[TD([subQ6])],"derivedFrom":makeQuery(id+"FKiHbmxaIrGreLf_1.3.F3.boolean.opBoolean","SPLIT",FACE,{"disambiguationData":[TD([subQ6])],"derivedFrom":makeQuery(id+"FKiHbmxaIrGreLf_1.2.F3.boolean.opBoolean","SPLIT",FACE,{"disambiguationData":[TD([subQ6])],"derivedFrom":makeQuery(id+"FKiHbmxaIrGreLf_1.1.F3.boolean.opBoolean","SPLIT",FACE,{"disambiguationData":[TD([subQ6])],"derivedFrom":makeQuery(id+"F1.opRevolve","SWEPT_FACE",FACE,{"disambiguationData":[OSD([sQuery(id+"F0.wireOp",EDGE,"E2")])]})})})})}),makeQuery(id+"FKiHbmxaIrGreLf_1.5.F3.opRevolve","CAP_FACE",FACE,{"disambiguationData":[OSD([subQ3,subQ2,subQ1,subQ0])],"isStart":false})]});}
            var Q30;
            {var subQ0=sQuery(id+"F2.wireOp",EDGE,"E13");var subQ1=sQuery(id+"F2.wireOp",EDGE,"E12");var subQ2=sQuery(id+"F2.wireOp",EDGE,"E11");var subQ3=sQuery(id+"F2.wireOp",EDGE,"E10");var subQ6=makeQuery(id+"F3.boolean.opBoolean","COPY",FACE,{"derivedFrom":makeQuery(id+"F3.opRevolve","CAP_FACE",FACE,{"disambiguationData":[OSD([subQ3,subQ2,subQ1,subQ0])],"isStart":true})});Q30=makeQuery(id+"FKiHbmxaIrGreLf_1.5.F3.boolean.opBoolean","INTERSECT",EDGE,{"derivedFrom":[makeQuery(id+"FKiHbmxaIrGreLf_1.4.F3.boolean.opBoolean","SPLIT",FACE,{"disambiguationData":[TD([subQ6])],"derivedFrom":makeQuery(id+"FKiHbmxaIrGreLf_1.3.F3.boolean.opBoolean","SPLIT",FACE,{"disambiguationData":[TD([subQ6])],"derivedFrom":makeQuery(id+"FKiHbmxaIrGreLf_1.2.F3.boolean.opBoolean","SPLIT",FACE,{"disambiguationData":[TD([subQ6])],"derivedFrom":makeQuery(id+"FKiHbmxaIrGreLf_1.1.F3.boolean.opBoolean","SPLIT",FACE,{"disambiguationData":[TD([subQ6])],"derivedFrom":makeQuery(id+"F1.opRevolve","SWEPT_FACE",FACE,{"disambiguationData":[OSD([sQuery(id+"F0.wireOp",EDGE,"E2")])]})})})})}),makeQuery(id+"FKiHbmxaIrGreLf_1.5.F3.opRevolve","CAP_FACE",FACE,{"disambiguationData":[OSD([subQ3,subQ2,subQ1,subQ0])],"isStart":true})]});}
            var Q31;
            {var subQ0=sQuery(id+"F2.wireOp",EDGE,"E13");var subQ1=sQuery(id+"F2.wireOp",EDGE,"E12");var subQ2=sQuery(id+"F2.wireOp",EDGE,"E11");var subQ3=sQuery(id+"F2.wireOp",EDGE,"E10");var subQ6=makeQuery(id+"F3.boolean.opBoolean","COPY",FACE,{"derivedFrom":makeQuery(id+"F3.opRevolve","CAP_FACE",FACE,{"disambiguationData":[OSD([subQ3,subQ2,subQ1,subQ0])],"isStart":true})});Q31=makeQuery(id+"FKiHbmxaIrGreLf_1.4.F3.boolean.opBoolean","INTERSECT",EDGE,{"derivedFrom":[makeQuery(id+"FKiHbmxaIrGreLf_1.3.F3.boolean.opBoolean","SPLIT",FACE,{"disambiguationData":[TD([subQ6])],"derivedFrom":makeQuery(id+"FKiHbmxaIrGreLf_1.2.F3.boolean.opBoolean","SPLIT",FACE,{"disambiguationData":[TD([subQ6])],"derivedFrom":makeQuery(id+"FKiHbmxaIrGreLf_1.1.F3.boolean.opBoolean","SPLIT",FACE,{"disambiguationData":[TD([subQ6])],"derivedFrom":makeQuery(id+"F1.opRevolve","SWEPT_FACE",FACE,{"disambiguationData":[OSD([sQuery(id+"F0.wireOp",EDGE,"E2")])]})})})}),makeQuery(id+"FKiHbmxaIrGreLf_1.4.F3.opRevolve","CAP_FACE",FACE,{"disambiguationData":[OSD([subQ3,subQ2,subQ1,subQ0])],"isStart":false})]});}
            var Q32;
            {var subQ0=sQuery(id+"F2.wireOp",EDGE,"E13");var subQ1=sQuery(id+"F2.wireOp",EDGE,"E12");var subQ2=sQuery(id+"F2.wireOp",EDGE,"E11");var subQ3=sQuery(id+"F2.wireOp",EDGE,"E10");var subQ6=makeQuery(id+"F3.boolean.opBoolean","COPY",FACE,{"derivedFrom":makeQuery(id+"F3.opRevolve","CAP_FACE",FACE,{"disambiguationData":[OSD([subQ3,subQ2,subQ1,subQ0])],"isStart":true})});Q32=makeQuery(id+"FKiHbmxaIrGreLf_1.4.F3.boolean.opBoolean","INTERSECT",EDGE,{"derivedFrom":[makeQuery(id+"FKiHbmxaIrGreLf_1.3.F3.boolean.opBoolean","SPLIT",FACE,{"disambiguationData":[TD([subQ6])],"derivedFrom":makeQuery(id+"FKiHbmxaIrGreLf_1.2.F3.boolean.opBoolean","SPLIT",FACE,{"disambiguationData":[TD([subQ6])],"derivedFrom":makeQuery(id+"FKiHbmxaIrGreLf_1.1.F3.boolean.opBoolean","SPLIT",FACE,{"disambiguationData":[TD([subQ6])],"derivedFrom":makeQuery(id+"F1.opRevolve","SWEPT_FACE",FACE,{"disambiguationData":[OSD([sQuery(id+"F0.wireOp",EDGE,"E2")])]})})})}),makeQuery(id+"FKiHbmxaIrGreLf_1.4.F3.opRevolve","CAP_FACE",FACE,{"disambiguationData":[OSD([subQ3,subQ2,subQ1,subQ0])],"isStart":true})]});}
            var Q33;
            {var subQ0=sQuery(id+"F2.wireOp",EDGE,"E13");var subQ1=sQuery(id+"F2.wireOp",EDGE,"E12");var subQ2=sQuery(id+"F2.wireOp",EDGE,"E11");var subQ3=sQuery(id+"F2.wireOp",EDGE,"E10");var subQ6=makeQuery(id+"F3.boolean.opBoolean","COPY",FACE,{"derivedFrom":makeQuery(id+"F3.opRevolve","CAP_FACE",FACE,{"disambiguationData":[OSD([subQ3,subQ2,subQ1,subQ0])],"isStart":true})});Q33=makeQuery(id+"FKiHbmxaIrGreLf_1.3.F3.boolean.opBoolean","INTERSECT",EDGE,{"derivedFrom":[makeQuery(id+"FKiHbmxaIrGreLf_1.2.F3.boolean.opBoolean","SPLIT",FACE,{"disambiguationData":[TD([subQ6])],"derivedFrom":makeQuery(id+"FKiHbmxaIrGreLf_1.1.F3.boolean.opBoolean","SPLIT",FACE,{"disambiguationData":[TD([subQ6])],"derivedFrom":makeQuery(id+"F1.opRevolve","SWEPT_FACE",FACE,{"disambiguationData":[OSD([sQuery(id+"F0.wireOp",EDGE,"E2")])]})})}),makeQuery(id+"FKiHbmxaIrGreLf_1.3.F3.opRevolve","CAP_FACE",FACE,{"disambiguationData":[OSD([subQ3,subQ2,subQ1,subQ0])],"isStart":false})]});}
            var Q34;
            {var subQ0=sQuery(id+"F2.wireOp",EDGE,"E13");var subQ1=sQuery(id+"F2.wireOp",EDGE,"E12");var subQ2=sQuery(id+"F2.wireOp",EDGE,"E11");var subQ3=sQuery(id+"F2.wireOp",EDGE,"E10");var subQ6=makeQuery(id+"F3.boolean.opBoolean","COPY",FACE,{"derivedFrom":makeQuery(id+"F3.opRevolve","CAP_FACE",FACE,{"disambiguationData":[OSD([subQ3,subQ2,subQ1,subQ0])],"isStart":true})});Q34=makeQuery(id+"FKiHbmxaIrGreLf_1.3.F3.boolean.opBoolean","INTERSECT",EDGE,{"derivedFrom":[makeQuery(id+"FKiHbmxaIrGreLf_1.2.F3.boolean.opBoolean","SPLIT",FACE,{"disambiguationData":[TD([subQ6])],"derivedFrom":makeQuery(id+"FKiHbmxaIrGreLf_1.1.F3.boolean.opBoolean","SPLIT",FACE,{"disambiguationData":[TD([subQ6])],"derivedFrom":makeQuery(id+"F1.opRevolve","SWEPT_FACE",FACE,{"disambiguationData":[OSD([sQuery(id+"F0.wireOp",EDGE,"E2")])]})})}),makeQuery(id+"FKiHbmxaIrGreLf_1.3.F3.opRevolve","CAP_FACE",FACE,{"disambiguationData":[OSD([subQ3,subQ2,subQ1,subQ0])],"isStart":true})]});}
            var Q35;
            {var subQ0=sQuery(id+"F2.wireOp",EDGE,"E13");var subQ1=sQuery(id+"F2.wireOp",EDGE,"E12");var subQ2=sQuery(id+"F2.wireOp",EDGE,"E11");var subQ3=sQuery(id+"F2.wireOp",EDGE,"E10");Q35=makeQuery(id+"FKiHbmxaIrGreLf_1.2.F3.boolean.opBoolean","INTERSECT",EDGE,{"derivedFrom":[makeQuery(id+"FKiHbmxaIrGreLf_1.1.F3.boolean.opBoolean","SPLIT",FACE,{"disambiguationData":[TD([makeQuery(id+"F3.boolean.opBoolean","COPY",FACE,{"derivedFrom":makeQuery(id+"F3.opRevolve","CAP_FACE",FACE,{"disambiguationData":[OSD([subQ3,subQ2,subQ1,subQ0])],"isStart":true})})])],"derivedFrom":makeQuery(id+"F1.opRevolve","SWEPT_FACE",FACE,{"disambiguationData":[OSD([sQuery(id+"F0.wireOp",EDGE,"E2")])]})}),makeQuery(id+"FKiHbmxaIrGreLf_1.2.F3.opRevolve","CAP_FACE",FACE,{"disambiguationData":[OSD([subQ3,subQ2,subQ1,subQ0])],"isStart":false})]});}
            var Q36;
            Q36=makeQuery(id+"FKiHbmxaIrGreLf_1.1.F3.boolean.opBoolean","INTERSECT",EDGE,{"derivedFrom":[makeQuery(id+"F1.opRevolve","SWEPT_FACE",FACE,{"disambiguationData":[OSD([sQuery(id+"F0.wireOp",EDGE,"E2")])]}),makeQuery(id+"FKiHbmxaIrGreLf_1.1.F3.opRevolve","CAP_FACE",FACE,{"disambiguationData":[OSD([sQuery(id+"F2.wireOp",EDGE,"E10"),sQuery(id+"F2.wireOp",EDGE,"E11"),sQuery(id+"F2.wireOp",EDGE,"E12"),sQuery(id+"F2.wireOp",EDGE,"E13")])],"isStart":false})]});
            var Q37;
            {var subQ0=sQuery(id+"F2.wireOp",EDGE,"E13");var subQ1=sQuery(id+"F2.wireOp",EDGE,"E12");var subQ2=sQuery(id+"F2.wireOp",EDGE,"E11");var subQ3=sQuery(id+"F2.wireOp",EDGE,"E10");Q37=makeQuery(id+"FKiHbmxaIrGreLf_1.2.F3.boolean.opBoolean","INTERSECT",EDGE,{"derivedFrom":[makeQuery(id+"FKiHbmxaIrGreLf_1.1.F3.boolean.opBoolean","SPLIT",FACE,{"disambiguationData":[TD([makeQuery(id+"F3.boolean.opBoolean","COPY",FACE,{"derivedFrom":makeQuery(id+"F3.opRevolve","CAP_FACE",FACE,{"disambiguationData":[OSD([subQ3,subQ2,subQ1,subQ0])],"isStart":true})})])],"derivedFrom":makeQuery(id+"F1.opRevolve","SWEPT_FACE",FACE,{"disambiguationData":[OSD([sQuery(id+"F0.wireOp",EDGE,"E2")])]})}),makeQuery(id+"FKiHbmxaIrGreLf_1.2.F3.opRevolve","CAP_FACE",FACE,{"disambiguationData":[OSD([subQ3,subQ2,subQ1,subQ0])],"isStart":true})]});}
            var Q38;
            Q38=makeQuery(id+"FKiHbmxaIrGreLf_1.1.F3.boolean.opBoolean","INTERSECT",EDGE,{"derivedFrom":[makeQuery(id+"F1.opRevolve","SWEPT_FACE",FACE,{"disambiguationData":[OSD([sQuery(id+"F0.wireOp",EDGE,"E2")])]}),makeQuery(id+"FKiHbmxaIrGreLf_1.1.F3.opRevolve","CAP_FACE",FACE,{"disambiguationData":[OSD([sQuery(id+"F2.wireOp",EDGE,"E10"),sQuery(id+"F2.wireOp",EDGE,"E11"),sQuery(id+"F2.wireOp",EDGE,"E12"),sQuery(id+"F2.wireOp",EDGE,"E13")])],"isStart":true})]});
            var Q39;
            Q39=makeQuery(id+"F3.boolean.opBoolean","INTERSECT",EDGE,{"derivedFrom":[makeQuery(id+"F1.opRevolve","SWEPT_FACE",FACE,{"disambiguationData":[OSD([sQuery(id+"F0.wireOp",EDGE,"E2")])]}),makeQuery(id+"F3.opRevolve","CAP_FACE",FACE,{"disambiguationData":[OSD([sQuery(id+"F2.wireOp",EDGE,"E10"),sQuery(id+"F2.wireOp",EDGE,"E11"),sQuery(id+"F2.wireOp",EDGE,"E12"),sQuery(id+"F2.wireOp",EDGE,"E13")])],"isStart":false})]});
            var Q40;
            Q40=makeQuery(id+"F1.opRevolve","SWEPT_FACE",FACE,{"disambiguationData":[OSD([sQuery(id+"F0.wireOp",EDGE,"E4")])]});
            fillet(context, id + "F4", {"entities" : qUnion([Q0, Q1, Q2, Q3, Q4, Q5, Q6, Q7, Q8, Q9, Q10, Q11, Q12, Q13, Q14, Q15, Q16, Q17, Q18, Q19, Q20, Q21, Q22, Q23, Q24, Q25, Q26, Q27, Q28, Q29, Q30, Q31, Q32, Q33, Q34, Q35, Q36, Q37, Q38, Q39, Q40]), "radius" : 2.5 * mm, "tangentPropagation" : true, "allowEdgeOverflow" : false});
        }
        {
            var Q0;
            Q0=qCreatedBy(makeId("Front.planeOp"),FACE);
            var sketch = newSketch(context, id + "F5", { "sketchPlane" : qUnion([Q0])});
            skLineSegment(sketch, "E14", {"start": v(-39, 0) * mm, "end": v(-41.17, 30) * mm});
            skLineSegment(sketch, "E15", {"start": v(-41.17, 30) * mm, "end": v(-45.52, 30) * mm});
            skFitSpline(sketch, "E16", {"points": [v(-45.52, 30) * mm, v(-53.28, 29.8) * mm, v(-56.87, 35.33) * mm, v(-59, 40) * mm], "startDerivative": vector(-22.61, -11.45) * mm, "endDerivative": vector(-9.77, 2.32) * mm});
            skLineSegment(sketch, "E17", {"start": v(-59, 40) * mm, "end": v(-64, 40) * mm});
            skLineSegment(sketch, "E18", {"start": v(-69, 35) * mm, "end": v(-69, 0) * mm});
            skLineSegment(sketch, "E19", {"start": v(-69, 0) * mm, "end": v(-39, 0) * mm});
            skPoint(sketch, "E20.visualSharp", {"position": v(-69, 40) * mm});
            skLineSegment(sketch, "E21", {"start": v(-64, 40) * mm, "end": v(-69, 40) * mm});
            skLineSegment(sketch, "E22", {"start": v(-69, 35) * mm, "end": v(-69, 40) * mm});
            skSolve(sketch);
        }
        {
            var Q0;
            Q0=makeQuery(id+"F5.imprint","IMPRINT",FACE,{"disambiguationData":[TD([[makeQuery(id+"F5.imprint","IMPRINT",EDGE,{"derivedFrom":sQuery(id+"F5.wireOp",EDGE,"E14")}),1.0]])]});
            var Q1;
            Q1=sQuery(id+"F0.wireOp",EDGE,"E7");
            revolve(context, id + "F6", {"operationType" : NewBodyOperationType.ADD, "surfaceOperationType" : NewSurfaceOperationType.NEW, "entities" : qUnion([Q0]), "axis" : qUnion([Q1]), "revolveType" : RevolveType.SYMMETRIC, "oppositeDirection" : true, "angle" : 10 * degree});
        }
        {
            var Q0;
            Q0=makeQuery(id+"F6.boolean.opBoolean","MERGE",FACE,{"derivedFrom":[makeQuery(id+"F1.opRevolve","SWEPT_FACE",FACE,{"disambiguationData":[OSD([sQuery(id+"F0.wireOp",EDGE,"E6")])]}),makeQuery(id+"F6.opRevolve","SWEPT_FACE",FACE,{"disambiguationData":[OSD([sQuery(id+"F5.wireOp",EDGE,"E19")])]})]});
            var sketch = newSketch(context, id + "F7", { "sketchPlane" : qUnion([Q0])});
            skLineSegment(sketch, "E23", {"start": v(-68.74, 6.01) * mm, "end": v(-58.78, 5.14) * mm});
            skArc(sketch, "E24", {"start": v(-58.78, 5.14) * mm, "mid": v(-63.32, 10.51) * mm, "end": v(-68.74, 6.01) * mm});
            skLineSegment(sketch, "E25.MirrorCS", {"start": v(-68.74, -6.01) * mm, "end": v(-58.78, -5.14) * mm});
            skArc(sketch, "E26.MirrorCS", {"start": v(-58.78, -5.14) * mm, "mid": v(-63.32, -10.51) * mm, "end": v(-68.74, -6.01) * mm});
            skSolve(sketch);
        }
        {
            var Q0;
            Q0 = qSketchRegion(id + "F7", true);
            extrude(context, id + "F8", {"entities" : qUnion([Q0]), "operationType" : NewBodyOperationType.ADD, "oppositeDirection" : true, "depth" : 40 * mm, "offsetDistance" : 25 * mm});
        }
        {
            var Q0;
            Q0=makeQuery(id+"F6.boolean.opBoolean","INTERSECT",EDGE,{"derivedFrom":[makeQuery(id+"F1.opRevolve","SWEPT_FACE",FACE,{"disambiguationData":[OSD([sQuery(id+"F0.wireOp",EDGE,"E5")])]}),makeQuery(id+"F6.opRevolve","CAP_FACE",FACE,{"disambiguationData":[OSD([sQuery(id+"F5.wireOp",EDGE,"E14"),sQuery(id+"F5.wireOp",EDGE,"E15"),sQuery(id+"F5.wireOp",EDGE,"E16"),sQuery(id+"F5.wireOp",EDGE,"E17"),sQuery(id+"F5.wireOp",EDGE,"E18"),sQuery(id+"F5.wireOp",EDGE,"E19"),sQuery(id+"F5.wireOp",EDGE,"E21"),sQuery(id+"F5.wireOp",EDGE,"E22")])],"isStart":false})]});
            var Q1;
            Q1=makeQuery(id+"F8.opExtrude","SWEPT_EDGE",EDGE,{"disambiguationData":[OSD([sQuery(id+"F5.wireOp",EDGE,"E19"),sQuery(id+"F7.wireOp",EDGE,"E25.MirrorCS"),sQuery(id+"F7.wireOp",EDGE,"E26.MirrorCS")])]});
            var Q2;
            Q2=makeQuery(id+"F6.boolean.opBoolean","INTERSECT",EDGE,{"derivedFrom":[makeQuery(id+"F1.opRevolve","SWEPT_FACE",FACE,{"disambiguationData":[OSD([sQuery(id+"F0.wireOp",EDGE,"E5")])]}),makeQuery(id+"F6.opRevolve","CAP_FACE",FACE,{"disambiguationData":[OSD([sQuery(id+"F5.wireOp",EDGE,"E14"),sQuery(id+"F5.wireOp",EDGE,"E15"),sQuery(id+"F5.wireOp",EDGE,"E16"),sQuery(id+"F5.wireOp",EDGE,"E17"),sQuery(id+"F5.wireOp",EDGE,"E18"),sQuery(id+"F5.wireOp",EDGE,"E19"),sQuery(id+"F5.wireOp",EDGE,"E21"),sQuery(id+"F5.wireOp",EDGE,"E22")])],"isStart":true})]});
            var Q3;
            Q3=makeQuery(id+"F8.opExtrude","SWEPT_EDGE",EDGE,{"disambiguationData":[OSD([sQuery(id+"F5.wireOp",EDGE,"E19"),sQuery(id+"F7.wireOp",EDGE,"E23"),sQuery(id+"F7.wireOp",EDGE,"E24")])]});
            fillet(context, id + "F9", {"entities" : qUnion([Q0, Q1, Q2, Q3]), "radius" : 5 * mm, "tangentPropagation" : true, "allowEdgeOverflow" : false});
        }
    });
